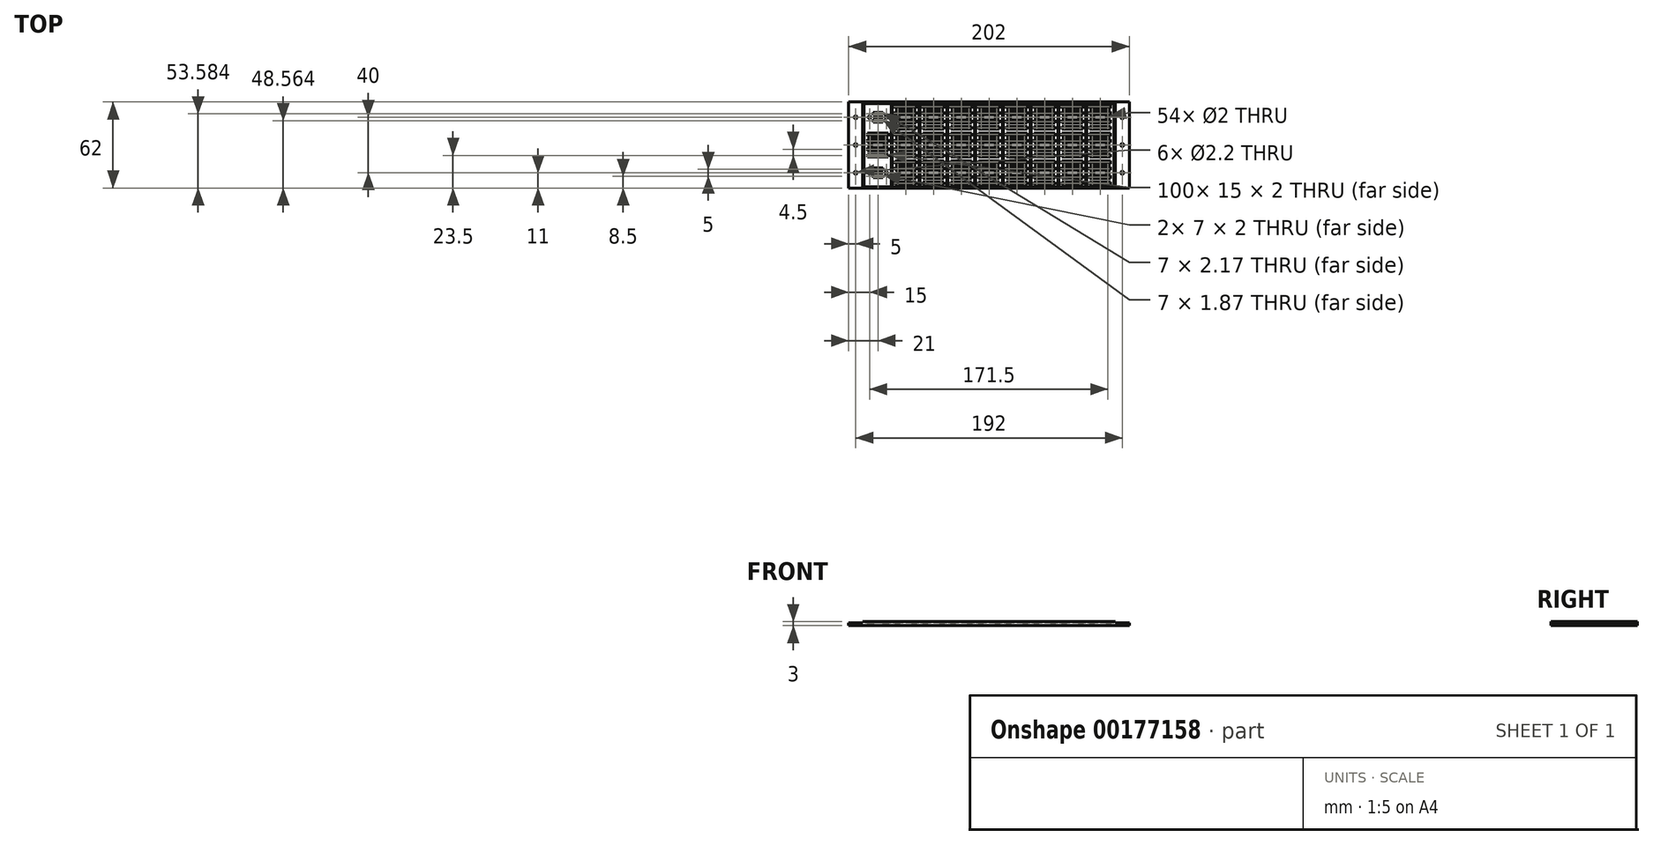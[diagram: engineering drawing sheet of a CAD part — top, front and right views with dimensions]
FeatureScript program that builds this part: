
annotation { "Feature Type Name" : "Feature", "Feature Type Description" : "" }
export const myFeature = defineFeature(function(context is Context, id is Id, definition is map)
    precondition{}
    {
        {
            var Q0;
            Q0=qCreatedBy(makeId("Top.planeOp"),FACE);
            var sketch = newSketch(context, id + "F0", { "sketchPlane" : qUnion([Q0])});
            skLineSegment(sketch, "E0.bottom", {"start": v(91, -31) * mm, "end": v(-91, -31) * mm});
            skLineSegment(sketch, "E0.top", {"start": v(91, 31) * mm, "end": v(-91, 31) * mm});
            skLineSegment(sketch, "E0.left", {"start": v(91, -31) * mm, "end": v(91, 31) * mm});
            skLineSegment(sketch, "E0.right", {"start": v(-91, -31) * mm, "end": v(-91, 31) * mm});
            skPoint(sketch, "E0.middle", {"position": v(0, 0) * mm});
            skSolve(sketch);
        }
        {
            var Q0;
            Q0 = qSketchRegion(id + "F0", true);
            extrude(context, id + "F1", {"entities" : qUnion([Q0]), "depth" : 2 * mm});
        }
        {
            var Q0;
            Q0=makeQuery(id+"F1.opExtrude","CAP_FACE",FACE,{"disambiguationData":[OSD([sQuery(id+"F0.wireOp",EDGE,"E0.bottom"),sQuery(id+"F0.wireOp",EDGE,"E0.top"),sQuery(id+"F0.wireOp",EDGE,"E0.left"),sQuery(id+"F0.wireOp",EDGE,"E0.right")])],"isStart":false});
            var sketch = newSketch(context, id + "F2", { "sketchPlane" : qUnion([Q0])});
            skLineSegment(sketch, "E1.bottom", {"start": v(91, -31) * mm, "end": v(-91, -31) * mm});
            skLineSegment(sketch, "E1.top", {"start": v(91, 31) * mm, "end": v(-91, 31) * mm});
            skLineSegment(sketch, "E1.left", {"start": v(91, -31) * mm, "end": v(91, 31) * mm});
            skLineSegment(sketch, "E1.right", {"start": v(-91, -31) * mm, "end": v(-91, 31) * mm});
            skPoint(sketch, "E1.middle", {"position": v(0, 0) * mm});
            skLineSegment(sketch, "E2.bottom", {"start": v(90, -30) * mm, "end": v(-90, -30) * mm});
            skLineSegment(sketch, "E2.top", {"start": v(90, 30) * mm, "end": v(-90, 30) * mm});
            skLineSegment(sketch, "E2.left", {"start": v(90, -30) * mm, "end": v(90, 30) * mm});
            skLineSegment(sketch, "E2.right", {"start": v(-90, -30) * mm, "end": v(-90, 30) * mm});
            skSolve(sketch);
        }
        {
            var Q0;
            Q0 = qSketchRegion(id + "F2", true);
            extrude(context, id + "F3", {"entities" : qUnion([Q0]), "operationType" : NewBodyOperationType.ADD, "depth" : 1 * mm});
        }
        {
            var Q0;
            Q0=qCreatedBy(makeId("Top.planeOp"),FACE);
            var sketch = newSketch(context, id + "F4", { "sketchPlane" : qUnion([Q0])});
            skLineSegment(sketch, "E3.bottom", {"start": v(-91, 31) * mm, "end": v(-101, 31) * mm});
            skLineSegment(sketch, "E3.top", {"start": v(-91, -31) * mm, "end": v(-101, -31) * mm});
            skLineSegment(sketch, "E3.left", {"start": v(-91, 31) * mm, "end": v(-91, -31) * mm});
            skLineSegment(sketch, "E3.right", {"start": v(-101, 31) * mm, "end": v(-101, -31) * mm});
            skLineSegment(sketch, "E4.bottom", {"start": v(91, 31) * mm, "end": v(101, 31) * mm});
            skLineSegment(sketch, "E4.top", {"start": v(91, -31) * mm, "end": v(101, -31) * mm});
            skLineSegment(sketch, "E4.left", {"start": v(91, 31) * mm, "end": v(91, -31) * mm});
            skLineSegment(sketch, "E4.right", {"start": v(101, 31) * mm, "end": v(101, -31) * mm});
            skCircle(sketch, "E5", {"center": v(-96, 20) * mm, "radius": 1.1 * mm});
            skPoint(sketch, "E5.centerSnap0", {"position": v(-96, 31) * mm});
            skCircle(sketch, "E6", {"center": v(-96, 0) * mm, "radius": 1.1 * mm});
            skCircle(sketch, "E7", {"center": v(-96, -20) * mm, "radius": 1.1 * mm});
            skCircle(sketch, "E8", {"center": v(96, 20) * mm, "radius": 1.1 * mm});
            skPoint(sketch, "E8.centerSnap0", {"position": v(96, 31) * mm});
            skCircle(sketch, "E9", {"center": v(96, 0) * mm, "radius": 1.1 * mm});
            skPoint(sketch, "E9.centerSnap0", {"position": v(91, 0) * mm});
            skCircle(sketch, "E10", {"center": v(96, -20) * mm, "radius": 1.1 * mm});
            skSolve(sketch);
        }
        {
            var Q0;
            Q0 = qSketchRegion(id + "F4", true);
            extrude(context, id + "F5", {"entities" : qUnion([Q0]), "operationType" : NewBodyOperationType.ADD, "depth" : 2 * mm});
        }
        {
            var Q0;
            Q0=makeQuery(id+"F5.boolean.opBoolean","MERGE",FACE,{"derivedFrom":[makeQuery(id+"F1.opExtrude","CAP_FACE",FACE,{"disambiguationData":[OSD([sQuery(id+"F0.wireOp",EDGE,"E0.bottom"),sQuery(id+"F0.wireOp",EDGE,"E0.top"),sQuery(id+"F0.wireOp",EDGE,"E0.left"),sQuery(id+"F0.wireOp",EDGE,"E0.right")])],"isStart":true}),makeQuery(id+"F5.opExtrude","CAP_FACE",FACE,{"disambiguationData":[OSD([sQuery(id+"F4.wireOp",EDGE,"E3.bottom"),sQuery(id+"F4.wireOp",EDGE,"E3.top"),sQuery(id+"F4.wireOp",EDGE,"E3.left"),sQuery(id+"F4.wireOp",EDGE,"E3.right"),sQuery(id+"F4.wireOp",EDGE,"E5"),sQuery(id+"F4.wireOp",EDGE,"E6"),sQuery(id+"F4.wireOp",EDGE,"E7")])],"isStart":true}),makeQuery(id+"F5.opExtrude","CAP_FACE",FACE,{"disambiguationData":[OSD([sQuery(id+"F4.wireOp",EDGE,"E4.bottom"),sQuery(id+"F4.wireOp",EDGE,"E4.top"),sQuery(id+"F4.wireOp",EDGE,"E4.left"),sQuery(id+"F4.wireOp",EDGE,"E4.right"),sQuery(id+"F4.wireOp",EDGE,"E8"),sQuery(id+"F4.wireOp",EDGE,"E9"),sQuery(id+"F4.wireOp",EDGE,"E10")])],"isStart":true})]});
            var sketch = newSketch(context, id + "F6", { "sketchPlane" : qUnion([Q0])});
            skCircle(sketch, "E11", {"center": v(74.5, 20) * mm, "radius": 1 * mm});
            skCircle(sketch, "E12", {"center": v(85.5, 20) * mm, "radius": 1 * mm});
            skLineSegment(sketch, "E13.bottom", {"start": v(87.5, 22) * mm, "end": v(72.5, 22) * mm});
            skLineSegment(sketch, "E13.top", {"start": v(87.5, 24) * mm, "end": v(72.5, 24) * mm});
            skLineSegment(sketch, "E13.left", {"start": v(87.5, 22) * mm, "end": v(87.5, 24) * mm});
            skLineSegment(sketch, "E13.right", {"start": v(72.5, 22) * mm, "end": v(72.5, 24) * mm});
            skPoint(sketch, "E13.middle", {"position": v(80, 23) * mm});
            skLineSegment(sketch, "E14.bottom", {"start": v(87.5, 26.5) * mm, "end": v(72.5, 26.5) * mm});
            skLineSegment(sketch, "E14.top", {"start": v(87.5, 28.5) * mm, "end": v(72.5, 28.5) * mm});
            skLineSegment(sketch, "E14.left", {"start": v(87.5, 26.5) * mm, "end": v(87.5, 28.5) * mm});
            skLineSegment(sketch, "E14.right", {"start": v(72.5, 26.5) * mm, "end": v(72.5, 28.5) * mm});
            skPoint(sketch, "E14.middle", {"position": v(80, 27.5) * mm});
            skLineSegment(sketch, "E15.bottom", {"start": v(87.5, 18) * mm, "end": v(72.5, 18) * mm});
            skLineSegment(sketch, "E15.top", {"start": v(87.5, 16) * mm, "end": v(72.5, 16) * mm});
            skLineSegment(sketch, "E15.left", {"start": v(87.5, 18) * mm, "end": v(87.5, 16) * mm});
            skLineSegment(sketch, "E15.right", {"start": v(72.5, 18) * mm, "end": v(72.5, 16) * mm});
            skPoint(sketch, "E15.middle", {"position": v(80, 17) * mm});
            skLineSegment(sketch, "E16.bottom", {"start": v(87.5, 13.5) * mm, "end": v(72.5, 13.5) * mm});
            skLineSegment(sketch, "E16.top", {"start": v(87.5, 11.5) * mm, "end": v(72.5, 11.5) * mm});
            skLineSegment(sketch, "E16.left", {"start": v(87.5, 13.5) * mm, "end": v(87.5, 11.5) * mm});
            skLineSegment(sketch, "E16.right", {"start": v(72.5, 13.5) * mm, "end": v(72.5, 11.5) * mm});
            skPoint(sketch, "E16.middle", {"position": v(80, 12.5) * mm});
            skLineSegment(sketch, "E17.bottom", {"start": v(89.5, 10.5) * mm, "end": v(70.5, 10.5) * mm, "construction": true});
            skLineSegment(sketch, "E17.top", {"start": v(89.5, 29.5) * mm, "end": v(70.5, 29.5) * mm, "construction": true});
            skLineSegment(sketch, "E17.left", {"start": v(89.5, 10.5) * mm, "end": v(89.5, 29.5) * mm, "construction": true});
            skLineSegment(sketch, "E17.right", {"start": v(70.5, 10.5) * mm, "end": v(70.5, 29.5) * mm, "construction": true});
            skPoint(sketch, "E17.middle", {"position": v(80, 20) * mm});
            skLineSegment(sketch, "E18.0.1.0", {"start": v(87.5, -8.5) * mm, "end": v(72.5, -8.5) * mm});
            skLineSegment(sketch, "E18.0.1.1", {"start": v(87.5, 8.5) * mm, "end": v(72.5, 8.5) * mm});
            skLineSegment(sketch, "E18.0.1.2", {"start": v(87.5, -4) * mm, "end": v(72.5, -4) * mm});
            skLineSegment(sketch, "E18.0.1.3", {"start": v(89.5, -9.5) * mm, "end": v(70.5, -9.5) * mm, "construction": true});
            skPoint(sketch, "E18.0.1.4", {"position": v(80, -3) * mm});
            skLineSegment(sketch, "E18.0.1.5", {"start": v(89.5, 9.5) * mm, "end": v(70.5, 9.5) * mm, "construction": true});
            skLineSegment(sketch, "E18.0.1.6", {"start": v(87.5, 6.5) * mm, "end": v(72.5, 6.5) * mm});
            skLineSegment(sketch, "E18.0.1.7", {"start": v(89.5, -9.5) * mm, "end": v(89.5, 9.5) * mm, "construction": true});
            skPoint(sketch, "E18.0.1.8", {"position": v(80, 3) * mm});
            skLineSegment(sketch, "E18.0.1.9", {"start": v(87.5, -6.5) * mm, "end": v(72.5, -6.5) * mm});
            skLineSegment(sketch, "E18.0.1.10", {"start": v(87.5, 4) * mm, "end": v(72.5, 4) * mm});
            skLineSegment(sketch, "E18.0.1.11", {"start": v(87.5, -2) * mm, "end": v(72.5, -2) * mm});
            skPoint(sketch, "E18.0.1.12", {"position": v(80, 7.5) * mm});
            skLineSegment(sketch, "E18.0.1.13", {"start": v(70.5, -9.5) * mm, "end": v(70.5, 9.5) * mm, "construction": true});
            skPoint(sketch, "E18.0.1.14", {"position": v(80, -7.5) * mm});
            skLineSegment(sketch, "E18.0.1.15", {"start": v(87.5, 2) * mm, "end": v(72.5, 2) * mm});
            skCircle(sketch, "E18.0.1.16", {"center": v(74.5, 0) * mm, "radius": 1 * mm});
            skCircle(sketch, "E18.0.1.17", {"center": v(85.5, 0) * mm, "radius": 1 * mm});
            skPoint(sketch, "E18.0.1.18", {"position": v(80, 0) * mm});
            skLineSegment(sketch, "E18.0.1.19", {"start": v(72.5, -6.5) * mm, "end": v(72.5, -8.5) * mm});
            skLineSegment(sketch, "E18.0.1.20", {"start": v(87.5, 6.5) * mm, "end": v(87.5, 8.5) * mm});
            skLineSegment(sketch, "E18.0.1.21", {"start": v(72.5, 6.5) * mm, "end": v(72.5, 8.5) * mm});
            skLineSegment(sketch, "E18.0.1.22", {"start": v(87.5, -2) * mm, "end": v(87.5, -4) * mm});
            skLineSegment(sketch, "E18.0.1.23", {"start": v(87.5, 2) * mm, "end": v(87.5, 4) * mm});
            skLineSegment(sketch, "E18.0.1.24", {"start": v(72.5, 2) * mm, "end": v(72.5, 4) * mm});
            skLineSegment(sketch, "E18.0.1.25", {"start": v(87.5, -6.5) * mm, "end": v(87.5, -8.5) * mm});
            skLineSegment(sketch, "E18.0.1.26", {"start": v(72.5, -2) * mm, "end": v(72.5, -4) * mm});
            skLineSegment(sketch, "E18.0.2.0", {"start": v(87.5, -28.5) * mm, "end": v(72.5, -28.5) * mm});
            skLineSegment(sketch, "E18.0.2.1", {"start": v(87.5, -11.5) * mm, "end": v(72.5, -11.5) * mm});
            skLineSegment(sketch, "E18.0.2.2", {"start": v(87.5, -24) * mm, "end": v(72.5, -24) * mm});
            skLineSegment(sketch, "E18.0.2.3", {"start": v(89.5, -29.5) * mm, "end": v(70.5, -29.5) * mm, "construction": true});
            skPoint(sketch, "E18.0.2.4", {"position": v(80, -23) * mm});
            skLineSegment(sketch, "E18.0.2.5", {"start": v(89.5, -10.5) * mm, "end": v(70.5, -10.5) * mm, "construction": true});
            skLineSegment(sketch, "E18.0.2.6", {"start": v(87.5, -13.5) * mm, "end": v(72.5, -13.5) * mm});
            skLineSegment(sketch, "E18.0.2.7", {"start": v(89.5, -29.5) * mm, "end": v(89.5, -10.5) * mm, "construction": true});
            skPoint(sketch, "E18.0.2.8", {"position": v(80, -17) * mm});
            skLineSegment(sketch, "E18.0.2.9", {"start": v(87.5, -26.5) * mm, "end": v(72.5, -26.5) * mm});
            skLineSegment(sketch, "E18.0.2.10", {"start": v(87.5, -16) * mm, "end": v(72.5, -16) * mm});
            skLineSegment(sketch, "E18.0.2.11", {"start": v(87.5, -22) * mm, "end": v(72.5, -22) * mm});
            skPoint(sketch, "E18.0.2.12", {"position": v(80, -12.5) * mm});
            skLineSegment(sketch, "E18.0.2.13", {"start": v(70.5, -29.5) * mm, "end": v(70.5, -10.5) * mm, "construction": true});
            skPoint(sketch, "E18.0.2.14", {"position": v(80, -27.5) * mm});
            skLineSegment(sketch, "E18.0.2.15", {"start": v(87.5, -18) * mm, "end": v(72.5, -18) * mm});
            skCircle(sketch, "E18.0.2.16", {"center": v(74.5, -20) * mm, "radius": 1 * mm});
            skCircle(sketch, "E18.0.2.17", {"center": v(85.5, -20) * mm, "radius": 1 * mm});
            skPoint(sketch, "E18.0.2.18", {"position": v(80, -20) * mm});
            skLineSegment(sketch, "E18.0.2.19", {"start": v(72.5, -26.5) * mm, "end": v(72.5, -28.5) * mm});
            skLineSegment(sketch, "E18.0.2.20", {"start": v(87.5, -13.5) * mm, "end": v(87.5, -11.5) * mm});
            skLineSegment(sketch, "E18.0.2.21", {"start": v(72.5, -13.5) * mm, "end": v(72.5, -11.5) * mm});
            skLineSegment(sketch, "E18.0.2.22", {"start": v(87.5, -22) * mm, "end": v(87.5, -24) * mm});
            skLineSegment(sketch, "E18.0.2.23", {"start": v(87.5, -18) * mm, "end": v(87.5, -16) * mm});
            skLineSegment(sketch, "E18.0.2.24", {"start": v(72.5, -18) * mm, "end": v(72.5, -16) * mm});
            skLineSegment(sketch, "E18.0.2.25", {"start": v(87.5, -26.5) * mm, "end": v(87.5, -28.5) * mm});
            skLineSegment(sketch, "E18.0.2.26", {"start": v(72.5, -22) * mm, "end": v(72.5, -24) * mm});
            skLineSegment(sketch, "E18.1.0.0", {"start": v(67.5, 11.5) * mm, "end": v(52.5, 11.5) * mm});
            skLineSegment(sketch, "E18.1.0.1", {"start": v(67.5, 28.5) * mm, "end": v(52.5, 28.5) * mm});
            skLineSegment(sketch, "E18.1.0.2", {"start": v(67.5, 16) * mm, "end": v(52.5, 16) * mm});
            skLineSegment(sketch, "E18.1.0.3", {"start": v(69.5, 10.5) * mm, "end": v(50.5, 10.5) * mm, "construction": true});
            skPoint(sketch, "E18.1.0.4", {"position": v(60, 17) * mm});
            skLineSegment(sketch, "E18.1.0.5", {"start": v(69.5, 29.5) * mm, "end": v(50.5, 29.5) * mm, "construction": true});
            skLineSegment(sketch, "E18.1.0.6", {"start": v(67.5, 26.5) * mm, "end": v(52.5, 26.5) * mm});
            skLineSegment(sketch, "E18.1.0.7", {"start": v(69.5, 10.5) * mm, "end": v(69.5, 29.5) * mm, "construction": true});
            skPoint(sketch, "E18.1.0.8", {"position": v(60, 23) * mm});
            skLineSegment(sketch, "E18.1.0.9", {"start": v(67.5, 13.5) * mm, "end": v(52.5, 13.5) * mm});
            skLineSegment(sketch, "E18.1.0.10", {"start": v(67.5, 24) * mm, "end": v(52.5, 24) * mm});
            skLineSegment(sketch, "E18.1.0.11", {"start": v(67.5, 18) * mm, "end": v(52.5, 18) * mm});
            skPoint(sketch, "E18.1.0.12", {"position": v(60, 27.5) * mm});
            skLineSegment(sketch, "E18.1.0.13", {"start": v(50.5, 10.5) * mm, "end": v(50.5, 29.5) * mm, "construction": true});
            skPoint(sketch, "E18.1.0.14", {"position": v(60, 12.5) * mm});
            skLineSegment(sketch, "E18.1.0.15", {"start": v(67.5, 22) * mm, "end": v(52.5, 22) * mm});
            skCircle(sketch, "E18.1.0.16", {"center": v(54.5, 20) * mm, "radius": 1 * mm});
            skCircle(sketch, "E18.1.0.17", {"center": v(65.5, 20) * mm, "radius": 1 * mm});
            skPoint(sketch, "E18.1.0.18", {"position": v(60, 20) * mm});
            skLineSegment(sketch, "E18.1.0.19", {"start": v(52.5, 13.5) * mm, "end": v(52.5, 11.5) * mm});
            skLineSegment(sketch, "E18.1.0.20", {"start": v(67.5, 26.5) * mm, "end": v(67.5, 28.5) * mm});
            skLineSegment(sketch, "E18.1.0.21", {"start": v(52.5, 26.5) * mm, "end": v(52.5, 28.5) * mm});
            skLineSegment(sketch, "E18.1.0.22", {"start": v(67.5, 18) * mm, "end": v(67.5, 16) * mm});
            skLineSegment(sketch, "E18.1.0.23", {"start": v(67.5, 22) * mm, "end": v(67.5, 24) * mm});
            skLineSegment(sketch, "E18.1.0.24", {"start": v(52.5, 22) * mm, "end": v(52.5, 24) * mm});
            skLineSegment(sketch, "E18.1.0.25", {"start": v(67.5, 13.5) * mm, "end": v(67.5, 11.5) * mm});
            skLineSegment(sketch, "E18.1.0.26", {"start": v(52.5, 18) * mm, "end": v(52.5, 16) * mm});
            skLineSegment(sketch, "E18.1.1.0", {"start": v(67.5, -8.5) * mm, "end": v(52.5, -8.5) * mm});
            skLineSegment(sketch, "E18.1.1.1", {"start": v(67.5, 8.5) * mm, "end": v(52.5, 8.5) * mm});
            skLineSegment(sketch, "E18.1.1.2", {"start": v(67.5, -4) * mm, "end": v(52.5, -4) * mm});
            skLineSegment(sketch, "E18.1.1.3", {"start": v(69.5, -9.5) * mm, "end": v(50.5, -9.5) * mm, "construction": true});
            skPoint(sketch, "E18.1.1.4", {"position": v(60, -3) * mm});
            skLineSegment(sketch, "E18.1.1.5", {"start": v(69.5, 9.5) * mm, "end": v(50.5, 9.5) * mm, "construction": true});
            skLineSegment(sketch, "E18.1.1.6", {"start": v(67.5, 6.5) * mm, "end": v(52.5, 6.5) * mm});
            skLineSegment(sketch, "E18.1.1.7", {"start": v(69.5, -9.5) * mm, "end": v(69.5, 9.5) * mm, "construction": true});
            skPoint(sketch, "E18.1.1.8", {"position": v(60, 3) * mm});
            skLineSegment(sketch, "E18.1.1.9", {"start": v(67.5, -6.5) * mm, "end": v(52.5, -6.5) * mm});
            skLineSegment(sketch, "E18.1.1.10", {"start": v(67.5, 4) * mm, "end": v(52.5, 4) * mm});
            skLineSegment(sketch, "E18.1.1.11", {"start": v(67.5, -2) * mm, "end": v(52.5, -2) * mm});
            skPoint(sketch, "E18.1.1.12", {"position": v(60, 7.5) * mm});
            skLineSegment(sketch, "E18.1.1.13", {"start": v(50.5, -9.5) * mm, "end": v(50.5, 9.5) * mm, "construction": true});
            skPoint(sketch, "E18.1.1.14", {"position": v(60, -7.5) * mm});
            skLineSegment(sketch, "E18.1.1.15", {"start": v(67.5, 2) * mm, "end": v(52.5, 2) * mm});
            skCircle(sketch, "E18.1.1.16", {"center": v(54.5, 0) * mm, "radius": 1 * mm});
            skCircle(sketch, "E18.1.1.17", {"center": v(65.5, 0) * mm, "radius": 1 * mm});
            skPoint(sketch, "E18.1.1.18", {"position": v(60, 0) * mm});
            skLineSegment(sketch, "E18.1.1.19", {"start": v(52.5, -6.5) * mm, "end": v(52.5, -8.5) * mm});
            skLineSegment(sketch, "E18.1.1.20", {"start": v(67.5, 6.5) * mm, "end": v(67.5, 8.5) * mm});
            skLineSegment(sketch, "E18.1.1.21", {"start": v(52.5, 6.5) * mm, "end": v(52.5, 8.5) * mm});
            skLineSegment(sketch, "E18.1.1.22", {"start": v(67.5, -2) * mm, "end": v(67.5, -4) * mm});
            skLineSegment(sketch, "E18.1.1.23", {"start": v(67.5, 2) * mm, "end": v(67.5, 4) * mm});
            skLineSegment(sketch, "E18.1.1.24", {"start": v(52.5, 2) * mm, "end": v(52.5, 4) * mm});
            skLineSegment(sketch, "E18.1.1.25", {"start": v(67.5, -6.5) * mm, "end": v(67.5, -8.5) * mm});
            skLineSegment(sketch, "E18.1.1.26", {"start": v(52.5, -2) * mm, "end": v(52.5, -4) * mm});
            skLineSegment(sketch, "E18.1.2.0", {"start": v(67.5, -28.5) * mm, "end": v(52.5, -28.5) * mm});
            skLineSegment(sketch, "E18.1.2.1", {"start": v(67.5, -11.5) * mm, "end": v(52.5, -11.5) * mm});
            skLineSegment(sketch, "E18.1.2.2", {"start": v(67.5, -24) * mm, "end": v(52.5, -24) * mm});
            skLineSegment(sketch, "E18.1.2.3", {"start": v(69.5, -29.5) * mm, "end": v(50.5, -29.5) * mm, "construction": true});
            skPoint(sketch, "E18.1.2.4", {"position": v(60, -23) * mm});
            skLineSegment(sketch, "E18.1.2.5", {"start": v(69.5, -10.5) * mm, "end": v(50.5, -10.5) * mm, "construction": true});
            skLineSegment(sketch, "E18.1.2.6", {"start": v(67.5, -13.5) * mm, "end": v(52.5, -13.5) * mm});
            skLineSegment(sketch, "E18.1.2.7", {"start": v(69.5, -29.5) * mm, "end": v(69.5, -10.5) * mm, "construction": true});
            skPoint(sketch, "E18.1.2.8", {"position": v(60, -17) * mm});
            skLineSegment(sketch, "E18.1.2.9", {"start": v(67.5, -26.5) * mm, "end": v(52.5, -26.5) * mm});
            skLineSegment(sketch, "E18.1.2.10", {"start": v(67.5, -16) * mm, "end": v(52.5, -16) * mm});
            skLineSegment(sketch, "E18.1.2.11", {"start": v(67.5, -22) * mm, "end": v(52.5, -22) * mm});
            skPoint(sketch, "E18.1.2.12", {"position": v(60, -12.5) * mm});
            skLineSegment(sketch, "E18.1.2.13", {"start": v(50.5, -29.5) * mm, "end": v(50.5, -10.5) * mm, "construction": true});
            skPoint(sketch, "E18.1.2.14", {"position": v(60, -27.5) * mm});
            skLineSegment(sketch, "E18.1.2.15", {"start": v(67.5, -18) * mm, "end": v(52.5, -18) * mm});
            skCircle(sketch, "E18.1.2.16", {"center": v(54.5, -20) * mm, "radius": 1 * mm});
            skCircle(sketch, "E18.1.2.17", {"center": v(65.5, -20) * mm, "radius": 1 * mm});
            skPoint(sketch, "E18.1.2.18", {"position": v(60, -20) * mm});
            skLineSegment(sketch, "E18.1.2.19", {"start": v(52.5, -26.5) * mm, "end": v(52.5, -28.5) * mm});
            skLineSegment(sketch, "E18.1.2.20", {"start": v(67.5, -13.5) * mm, "end": v(67.5, -11.5) * mm});
            skLineSegment(sketch, "E18.1.2.21", {"start": v(52.5, -13.5) * mm, "end": v(52.5, -11.5) * mm});
            skLineSegment(sketch, "E18.1.2.22", {"start": v(67.5, -22) * mm, "end": v(67.5, -24) * mm});
            skLineSegment(sketch, "E18.1.2.23", {"start": v(67.5, -18) * mm, "end": v(67.5, -16) * mm});
            skLineSegment(sketch, "E18.1.2.24", {"start": v(52.5, -18) * mm, "end": v(52.5, -16) * mm});
            skLineSegment(sketch, "E18.1.2.25", {"start": v(67.5, -26.5) * mm, "end": v(67.5, -28.5) * mm});
            skLineSegment(sketch, "E18.1.2.26", {"start": v(52.5, -22) * mm, "end": v(52.5, -24) * mm});
            skLineSegment(sketch, "E18.2.0.0", {"start": v(47.5, 11.5) * mm, "end": v(32.5, 11.5) * mm});
            skLineSegment(sketch, "E18.2.0.1", {"start": v(47.5, 28.5) * mm, "end": v(32.5, 28.5) * mm});
            skLineSegment(sketch, "E18.2.0.2", {"start": v(47.5, 16) * mm, "end": v(32.5, 16) * mm});
            skLineSegment(sketch, "E18.2.0.3", {"start": v(49.5, 10.5) * mm, "end": v(30.5, 10.5) * mm, "construction": true});
            skPoint(sketch, "E18.2.0.4", {"position": v(40, 17) * mm});
            skLineSegment(sketch, "E18.2.0.5", {"start": v(49.5, 29.5) * mm, "end": v(30.5, 29.5) * mm, "construction": true});
            skLineSegment(sketch, "E18.2.0.6", {"start": v(47.5, 26.5) * mm, "end": v(32.5, 26.5) * mm});
            skLineSegment(sketch, "E18.2.0.7", {"start": v(49.5, 10.5) * mm, "end": v(49.5, 29.5) * mm, "construction": true});
            skPoint(sketch, "E18.2.0.8", {"position": v(40, 23) * mm});
            skLineSegment(sketch, "E18.2.0.9", {"start": v(47.5, 13.5) * mm, "end": v(32.5, 13.5) * mm});
            skLineSegment(sketch, "E18.2.0.10", {"start": v(47.5, 24) * mm, "end": v(32.5, 24) * mm});
            skLineSegment(sketch, "E18.2.0.11", {"start": v(47.5, 18) * mm, "end": v(32.5, 18) * mm});
            skPoint(sketch, "E18.2.0.12", {"position": v(40, 27.5) * mm});
            skLineSegment(sketch, "E18.2.0.13", {"start": v(30.5, 10.5) * mm, "end": v(30.5, 29.5) * mm, "construction": true});
            skPoint(sketch, "E18.2.0.14", {"position": v(40, 12.5) * mm});
            skLineSegment(sketch, "E18.2.0.15", {"start": v(47.5, 22) * mm, "end": v(32.5, 22) * mm});
            skCircle(sketch, "E18.2.0.16", {"center": v(34.5, 20) * mm, "radius": 1 * mm});
            skCircle(sketch, "E18.2.0.17", {"center": v(45.5, 20) * mm, "radius": 1 * mm});
            skPoint(sketch, "E18.2.0.18", {"position": v(40, 20) * mm});
            skLineSegment(sketch, "E18.2.0.19", {"start": v(32.5, 13.5) * mm, "end": v(32.5, 11.5) * mm});
            skLineSegment(sketch, "E18.2.0.20", {"start": v(47.5, 26.5) * mm, "end": v(47.5, 28.5) * mm});
            skLineSegment(sketch, "E18.2.0.21", {"start": v(32.5, 26.5) * mm, "end": v(32.5, 28.5) * mm});
            skLineSegment(sketch, "E18.2.0.22", {"start": v(47.5, 18) * mm, "end": v(47.5, 16) * mm});
            skLineSegment(sketch, "E18.2.0.23", {"start": v(47.5, 22) * mm, "end": v(47.5, 24) * mm});
            skLineSegment(sketch, "E18.2.0.24", {"start": v(32.5, 22) * mm, "end": v(32.5, 24) * mm});
            skLineSegment(sketch, "E18.2.0.25", {"start": v(47.5, 13.5) * mm, "end": v(47.5, 11.5) * mm});
            skLineSegment(sketch, "E18.2.0.26", {"start": v(32.5, 18) * mm, "end": v(32.5, 16) * mm});
            skLineSegment(sketch, "E18.2.1.0", {"start": v(47.5, -8.5) * mm, "end": v(32.5, -8.5) * mm});
            skLineSegment(sketch, "E18.2.1.1", {"start": v(47.5, 8.5) * mm, "end": v(32.5, 8.5) * mm});
            skLineSegment(sketch, "E18.2.1.2", {"start": v(47.5, -4) * mm, "end": v(32.5, -4) * mm});
            skLineSegment(sketch, "E18.2.1.3", {"start": v(49.5, -9.5) * mm, "end": v(30.5, -9.5) * mm, "construction": true});
            skPoint(sketch, "E18.2.1.4", {"position": v(40, -3) * mm});
            skLineSegment(sketch, "E18.2.1.5", {"start": v(49.5, 9.5) * mm, "end": v(30.5, 9.5) * mm, "construction": true});
            skLineSegment(sketch, "E18.2.1.6", {"start": v(47.5, 6.5) * mm, "end": v(32.5, 6.5) * mm});
            skLineSegment(sketch, "E18.2.1.7", {"start": v(49.5, -9.5) * mm, "end": v(49.5, 9.5) * mm, "construction": true});
            skPoint(sketch, "E18.2.1.8", {"position": v(40, 3) * mm});
            skLineSegment(sketch, "E18.2.1.9", {"start": v(47.5, -6.5) * mm, "end": v(32.5, -6.5) * mm});
            skLineSegment(sketch, "E18.2.1.10", {"start": v(47.5, 4) * mm, "end": v(32.5, 4) * mm});
            skLineSegment(sketch, "E18.2.1.11", {"start": v(47.5, -2) * mm, "end": v(32.5, -2) * mm});
            skPoint(sketch, "E18.2.1.12", {"position": v(40, 7.5) * mm});
            skLineSegment(sketch, "E18.2.1.13", {"start": v(30.5, -9.5) * mm, "end": v(30.5, 9.5) * mm, "construction": true});
            skPoint(sketch, "E18.2.1.14", {"position": v(40, -7.5) * mm});
            skLineSegment(sketch, "E18.2.1.15", {"start": v(47.5, 2) * mm, "end": v(32.5, 2) * mm});
            skCircle(sketch, "E18.2.1.16", {"center": v(34.5, 0) * mm, "radius": 1 * mm});
            skCircle(sketch, "E18.2.1.17", {"center": v(45.5, 0) * mm, "radius": 1 * mm});
            skPoint(sketch, "E18.2.1.18", {"position": v(40, 0) * mm});
            skLineSegment(sketch, "E18.2.1.19", {"start": v(32.5, -6.5) * mm, "end": v(32.5, -8.5) * mm});
            skLineSegment(sketch, "E18.2.1.20", {"start": v(47.5, 6.5) * mm, "end": v(47.5, 8.5) * mm});
            skLineSegment(sketch, "E18.2.1.21", {"start": v(32.5, 6.5) * mm, "end": v(32.5, 8.5) * mm});
            skLineSegment(sketch, "E18.2.1.22", {"start": v(47.5, -2) * mm, "end": v(47.5, -4) * mm});
            skLineSegment(sketch, "E18.2.1.23", {"start": v(47.5, 2) * mm, "end": v(47.5, 4) * mm});
            skLineSegment(sketch, "E18.2.1.24", {"start": v(32.5, 2) * mm, "end": v(32.5, 4) * mm});
            skLineSegment(sketch, "E18.2.1.25", {"start": v(47.5, -6.5) * mm, "end": v(47.5, -8.5) * mm});
            skLineSegment(sketch, "E18.2.1.26", {"start": v(32.5, -2) * mm, "end": v(32.5, -4) * mm});
            skLineSegment(sketch, "E18.2.2.0", {"start": v(47.5, -28.5) * mm, "end": v(32.5, -28.5) * mm});
            skLineSegment(sketch, "E18.2.2.1", {"start": v(47.5, -11.5) * mm, "end": v(32.5, -11.5) * mm});
            skLineSegment(sketch, "E18.2.2.2", {"start": v(47.5, -24) * mm, "end": v(32.5, -24) * mm});
            skLineSegment(sketch, "E18.2.2.3", {"start": v(49.5, -29.5) * mm, "end": v(30.5, -29.5) * mm, "construction": true});
            skPoint(sketch, "E18.2.2.4", {"position": v(40, -23) * mm});
            skLineSegment(sketch, "E18.2.2.5", {"start": v(49.5, -10.5) * mm, "end": v(30.5, -10.5) * mm, "construction": true});
            skLineSegment(sketch, "E18.2.2.6", {"start": v(47.5, -13.5) * mm, "end": v(32.5, -13.5) * mm});
            skLineSegment(sketch, "E18.2.2.7", {"start": v(49.5, -29.5) * mm, "end": v(49.5, -10.5) * mm, "construction": true});
            skPoint(sketch, "E18.2.2.8", {"position": v(40, -17) * mm});
            skLineSegment(sketch, "E18.2.2.9", {"start": v(47.5, -26.5) * mm, "end": v(32.5, -26.5) * mm});
            skLineSegment(sketch, "E18.2.2.10", {"start": v(47.5, -16) * mm, "end": v(32.5, -16) * mm});
            skLineSegment(sketch, "E18.2.2.11", {"start": v(47.5, -22) * mm, "end": v(32.5, -22) * mm});
            skPoint(sketch, "E18.2.2.12", {"position": v(40, -12.5) * mm});
            skLineSegment(sketch, "E18.2.2.13", {"start": v(30.5, -29.5) * mm, "end": v(30.5, -10.5) * mm, "construction": true});
            skPoint(sketch, "E18.2.2.14", {"position": v(40, -27.5) * mm});
            skLineSegment(sketch, "E18.2.2.15", {"start": v(47.5, -18) * mm, "end": v(32.5, -18) * mm});
            skCircle(sketch, "E18.2.2.16", {"center": v(34.5, -20) * mm, "radius": 1 * mm});
            skCircle(sketch, "E18.2.2.17", {"center": v(45.5, -20) * mm, "radius": 1 * mm});
            skPoint(sketch, "E18.2.2.18", {"position": v(40, -20) * mm});
            skLineSegment(sketch, "E18.2.2.19", {"start": v(32.5, -26.5) * mm, "end": v(32.5, -28.5) * mm});
            skLineSegment(sketch, "E18.2.2.20", {"start": v(47.5, -13.5) * mm, "end": v(47.5, -11.5) * mm});
            skLineSegment(sketch, "E18.2.2.21", {"start": v(32.5, -13.5) * mm, "end": v(32.5, -11.5) * mm});
            skLineSegment(sketch, "E18.2.2.22", {"start": v(47.5, -22) * mm, "end": v(47.5, -24) * mm});
            skLineSegment(sketch, "E18.2.2.23", {"start": v(47.5, -18) * mm, "end": v(47.5, -16) * mm});
            skLineSegment(sketch, "E18.2.2.24", {"start": v(32.5, -18) * mm, "end": v(32.5, -16) * mm});
            skLineSegment(sketch, "E18.2.2.25", {"start": v(47.5, -26.5) * mm, "end": v(47.5, -28.5) * mm});
            skLineSegment(sketch, "E18.2.2.26", {"start": v(32.5, -22) * mm, "end": v(32.5, -24) * mm});
            skLineSegment(sketch, "E18.3.0.0", {"start": v(27.5, 11.5) * mm, "end": v(12.5, 11.5) * mm});
            skLineSegment(sketch, "E18.3.0.1", {"start": v(27.5, 28.5) * mm, "end": v(12.5, 28.5) * mm});
            skLineSegment(sketch, "E18.3.0.2", {"start": v(27.5, 16) * mm, "end": v(12.5, 16) * mm});
            skLineSegment(sketch, "E18.3.0.3", {"start": v(29.5, 10.5) * mm, "end": v(10.5, 10.5) * mm, "construction": true});
            skPoint(sketch, "E18.3.0.4", {"position": v(20, 17) * mm});
            skLineSegment(sketch, "E18.3.0.5", {"start": v(29.5, 29.5) * mm, "end": v(10.5, 29.5) * mm, "construction": true});
            skLineSegment(sketch, "E18.3.0.6", {"start": v(27.5, 26.5) * mm, "end": v(12.5, 26.5) * mm});
            skLineSegment(sketch, "E18.3.0.7", {"start": v(29.5, 10.5) * mm, "end": v(29.5, 29.5) * mm, "construction": true});
            skPoint(sketch, "E18.3.0.8", {"position": v(20, 23) * mm});
            skLineSegment(sketch, "E18.3.0.9", {"start": v(27.5, 13.5) * mm, "end": v(12.5, 13.5) * mm});
            skLineSegment(sketch, "E18.3.0.10", {"start": v(27.5, 24) * mm, "end": v(12.5, 24) * mm});
            skLineSegment(sketch, "E18.3.0.11", {"start": v(27.5, 18) * mm, "end": v(12.5, 18) * mm});
            skPoint(sketch, "E18.3.0.12", {"position": v(20, 27.5) * mm});
            skLineSegment(sketch, "E18.3.0.13", {"start": v(10.5, 10.5) * mm, "end": v(10.5, 29.5) * mm, "construction": true});
            skPoint(sketch, "E18.3.0.14", {"position": v(20, 12.5) * mm});
            skLineSegment(sketch, "E18.3.0.15", {"start": v(27.5, 22) * mm, "end": v(12.5, 22) * mm});
            skCircle(sketch, "E18.3.0.16", {"center": v(14.5, 20) * mm, "radius": 1 * mm});
            skCircle(sketch, "E18.3.0.17", {"center": v(25.5, 20) * mm, "radius": 1 * mm});
            skPoint(sketch, "E18.3.0.18", {"position": v(20, 20) * mm});
            skLineSegment(sketch, "E18.3.0.19", {"start": v(12.5, 13.5) * mm, "end": v(12.5, 11.5) * mm});
            skLineSegment(sketch, "E18.3.0.20", {"start": v(27.5, 26.5) * mm, "end": v(27.5, 28.5) * mm});
            skLineSegment(sketch, "E18.3.0.21", {"start": v(12.5, 26.5) * mm, "end": v(12.5, 28.5) * mm});
            skLineSegment(sketch, "E18.3.0.22", {"start": v(27.5, 18) * mm, "end": v(27.5, 16) * mm});
            skLineSegment(sketch, "E18.3.0.23", {"start": v(27.5, 22) * mm, "end": v(27.5, 24) * mm});
            skLineSegment(sketch, "E18.3.0.24", {"start": v(12.5, 22) * mm, "end": v(12.5, 24) * mm});
            skLineSegment(sketch, "E18.3.0.25", {"start": v(27.5, 13.5) * mm, "end": v(27.5, 11.5) * mm});
            skLineSegment(sketch, "E18.3.0.26", {"start": v(12.5, 18) * mm, "end": v(12.5, 16) * mm});
            skLineSegment(sketch, "E18.3.1.0", {"start": v(27.5, -8.5) * mm, "end": v(12.5, -8.5) * mm});
            skLineSegment(sketch, "E18.3.1.1", {"start": v(27.5, 8.5) * mm, "end": v(12.5, 8.5) * mm});
            skLineSegment(sketch, "E18.3.1.2", {"start": v(27.5, -4) * mm, "end": v(12.5, -4) * mm});
            skLineSegment(sketch, "E18.3.1.3", {"start": v(29.5, -9.5) * mm, "end": v(10.5, -9.5) * mm, "construction": true});
            skPoint(sketch, "E18.3.1.4", {"position": v(20, -3) * mm});
            skLineSegment(sketch, "E18.3.1.5", {"start": v(29.5, 9.5) * mm, "end": v(10.5, 9.5) * mm, "construction": true});
            skLineSegment(sketch, "E18.3.1.6", {"start": v(27.5, 6.5) * mm, "end": v(12.5, 6.5) * mm});
            skLineSegment(sketch, "E18.3.1.7", {"start": v(29.5, -9.5) * mm, "end": v(29.5, 9.5) * mm, "construction": true});
            skPoint(sketch, "E18.3.1.8", {"position": v(20, 3) * mm});
            skLineSegment(sketch, "E18.3.1.9", {"start": v(27.5, -6.5) * mm, "end": v(12.5, -6.5) * mm});
            skLineSegment(sketch, "E18.3.1.10", {"start": v(27.5, 4) * mm, "end": v(12.5, 4) * mm});
            skLineSegment(sketch, "E18.3.1.11", {"start": v(27.5, -2) * mm, "end": v(12.5, -2) * mm});
            skPoint(sketch, "E18.3.1.12", {"position": v(20, 7.5) * mm});
            skLineSegment(sketch, "E18.3.1.13", {"start": v(10.5, -9.5) * mm, "end": v(10.5, 9.5) * mm, "construction": true});
            skPoint(sketch, "E18.3.1.14", {"position": v(20, -7.5) * mm});
            skLineSegment(sketch, "E18.3.1.15", {"start": v(27.5, 2) * mm, "end": v(12.5, 2) * mm});
            skCircle(sketch, "E18.3.1.16", {"center": v(14.5, 0) * mm, "radius": 1 * mm});
            skCircle(sketch, "E18.3.1.17", {"center": v(25.5, 0) * mm, "radius": 1 * mm});
            skPoint(sketch, "E18.3.1.18", {"position": v(20, 0) * mm});
            skLineSegment(sketch, "E18.3.1.19", {"start": v(12.5, -6.5) * mm, "end": v(12.5, -8.5) * mm});
            skLineSegment(sketch, "E18.3.1.20", {"start": v(27.5, 6.5) * mm, "end": v(27.5, 8.5) * mm});
            skLineSegment(sketch, "E18.3.1.21", {"start": v(12.5, 6.5) * mm, "end": v(12.5, 8.5) * mm});
            skLineSegment(sketch, "E18.3.1.22", {"start": v(27.5, -2) * mm, "end": v(27.5, -4) * mm});
            skLineSegment(sketch, "E18.3.1.23", {"start": v(27.5, 2) * mm, "end": v(27.5, 4) * mm});
            skLineSegment(sketch, "E18.3.1.24", {"start": v(12.5, 2) * mm, "end": v(12.5, 4) * mm});
            skLineSegment(sketch, "E18.3.1.25", {"start": v(27.5, -6.5) * mm, "end": v(27.5, -8.5) * mm});
            skLineSegment(sketch, "E18.3.1.26", {"start": v(12.5, -2) * mm, "end": v(12.5, -4) * mm});
            skLineSegment(sketch, "E18.3.2.0", {"start": v(27.5, -28.5) * mm, "end": v(12.5, -28.5) * mm});
            skLineSegment(sketch, "E18.3.2.1", {"start": v(27.5, -11.5) * mm, "end": v(12.5, -11.5) * mm});
            skLineSegment(sketch, "E18.3.2.2", {"start": v(27.5, -24) * mm, "end": v(12.5, -24) * mm});
            skLineSegment(sketch, "E18.3.2.3", {"start": v(29.5, -29.5) * mm, "end": v(10.5, -29.5) * mm, "construction": true});
            skPoint(sketch, "E18.3.2.4", {"position": v(20, -23) * mm});
            skLineSegment(sketch, "E18.3.2.5", {"start": v(29.5, -10.5) * mm, "end": v(10.5, -10.5) * mm, "construction": true});
            skLineSegment(sketch, "E18.3.2.6", {"start": v(27.5, -13.5) * mm, "end": v(12.5, -13.5) * mm});
            skLineSegment(sketch, "E18.3.2.7", {"start": v(29.5, -29.5) * mm, "end": v(29.5, -10.5) * mm, "construction": true});
            skPoint(sketch, "E18.3.2.8", {"position": v(20, -17) * mm});
            skLineSegment(sketch, "E18.3.2.9", {"start": v(27.5, -26.5) * mm, "end": v(12.5, -26.5) * mm});
            skLineSegment(sketch, "E18.3.2.10", {"start": v(27.5, -16) * mm, "end": v(12.5, -16) * mm});
            skLineSegment(sketch, "E18.3.2.11", {"start": v(27.5, -22) * mm, "end": v(12.5, -22) * mm});
            skPoint(sketch, "E18.3.2.12", {"position": v(20, -12.5) * mm});
            skLineSegment(sketch, "E18.3.2.13", {"start": v(10.5, -29.5) * mm, "end": v(10.5, -10.5) * mm, "construction": true});
            skPoint(sketch, "E18.3.2.14", {"position": v(20, -27.5) * mm});
            skLineSegment(sketch, "E18.3.2.15", {"start": v(27.5, -18) * mm, "end": v(12.5, -18) * mm});
            skCircle(sketch, "E18.3.2.16", {"center": v(14.5, -20) * mm, "radius": 1 * mm});
            skCircle(sketch, "E18.3.2.17", {"center": v(25.5, -20) * mm, "radius": 1 * mm});
            skPoint(sketch, "E18.3.2.18", {"position": v(20, -20) * mm});
            skLineSegment(sketch, "E18.3.2.19", {"start": v(12.5, -26.5) * mm, "end": v(12.5, -28.5) * mm});
            skLineSegment(sketch, "E18.3.2.20", {"start": v(27.5, -13.5) * mm, "end": v(27.5, -11.5) * mm});
            skLineSegment(sketch, "E18.3.2.21", {"start": v(12.5, -13.5) * mm, "end": v(12.5, -11.5) * mm});
            skLineSegment(sketch, "E18.3.2.22", {"start": v(27.5, -22) * mm, "end": v(27.5, -24) * mm});
            skLineSegment(sketch, "E18.3.2.23", {"start": v(27.5, -18) * mm, "end": v(27.5, -16) * mm});
            skLineSegment(sketch, "E18.3.2.24", {"start": v(12.5, -18) * mm, "end": v(12.5, -16) * mm});
            skLineSegment(sketch, "E18.3.2.25", {"start": v(27.5, -26.5) * mm, "end": v(27.5, -28.5) * mm});
            skLineSegment(sketch, "E18.3.2.26", {"start": v(12.5, -22) * mm, "end": v(12.5, -24) * mm});
            skLineSegment(sketch, "E18.4.0.0", {"start": v(7.5, 11.5) * mm, "end": v(-7.5, 11.5) * mm});
            skLineSegment(sketch, "E18.4.0.1", {"start": v(7.5, 28.5) * mm, "end": v(-7.5, 28.5) * mm});
            skLineSegment(sketch, "E18.4.0.2", {"start": v(7.5, 16) * mm, "end": v(-7.5, 16) * mm});
            skLineSegment(sketch, "E18.4.0.3", {"start": v(9.5, 10.5) * mm, "end": v(-9.5, 10.5) * mm, "construction": true});
            skPoint(sketch, "E18.4.0.4", {"position": v(0, 17) * mm});
            skLineSegment(sketch, "E18.4.0.5", {"start": v(9.5, 29.5) * mm, "end": v(-9.5, 29.5) * mm, "construction": true});
            skLineSegment(sketch, "E18.4.0.6", {"start": v(7.5, 26.5) * mm, "end": v(-7.5, 26.5) * mm});
            skLineSegment(sketch, "E18.4.0.7", {"start": v(9.5, 10.5) * mm, "end": v(9.5, 29.5) * mm, "construction": true});
            skPoint(sketch, "E18.4.0.8", {"position": v(0, 23) * mm});
            skLineSegment(sketch, "E18.4.0.9", {"start": v(7.5, 13.5) * mm, "end": v(-7.5, 13.5) * mm});
            skLineSegment(sketch, "E18.4.0.10", {"start": v(7.5, 24) * mm, "end": v(-7.5, 24) * mm});
            skLineSegment(sketch, "E18.4.0.11", {"start": v(7.5, 18) * mm, "end": v(-7.5, 18) * mm});
            skPoint(sketch, "E18.4.0.12", {"position": v(0, 27.5) * mm});
            skLineSegment(sketch, "E18.4.0.13", {"start": v(-9.5, 10.5) * mm, "end": v(-9.5, 29.5) * mm, "construction": true});
            skPoint(sketch, "E18.4.0.14", {"position": v(0, 12.5) * mm});
            skLineSegment(sketch, "E18.4.0.15", {"start": v(7.5, 22) * mm, "end": v(-7.5, 22) * mm});
            skCircle(sketch, "E18.4.0.16", {"center": v(-5.5, 20) * mm, "radius": 1 * mm});
            skCircle(sketch, "E18.4.0.17", {"center": v(5.5, 20) * mm, "radius": 1 * mm});
            skPoint(sketch, "E18.4.0.18", {"position": v(0, 20) * mm});
            skLineSegment(sketch, "E18.4.0.19", {"start": v(-7.5, 13.5) * mm, "end": v(-7.5, 11.5) * mm});
            skLineSegment(sketch, "E18.4.0.20", {"start": v(7.5, 26.5) * mm, "end": v(7.5, 28.5) * mm});
            skLineSegment(sketch, "E18.4.0.21", {"start": v(-7.5, 26.5) * mm, "end": v(-7.5, 28.5) * mm});
            skLineSegment(sketch, "E18.4.0.22", {"start": v(7.5, 18) * mm, "end": v(7.5, 16) * mm});
            skLineSegment(sketch, "E18.4.0.23", {"start": v(7.5, 22) * mm, "end": v(7.5, 24) * mm});
            skLineSegment(sketch, "E18.4.0.24", {"start": v(-7.5, 22) * mm, "end": v(-7.5, 24) * mm});
            skLineSegment(sketch, "E18.4.0.25", {"start": v(7.5, 13.5) * mm, "end": v(7.5, 11.5) * mm});
            skLineSegment(sketch, "E18.4.0.26", {"start": v(-7.5, 18) * mm, "end": v(-7.5, 16) * mm});
            skLineSegment(sketch, "E18.4.1.0", {"start": v(7.5, -8.5) * mm, "end": v(-7.5, -8.5) * mm});
            skLineSegment(sketch, "E18.4.1.1", {"start": v(7.5, 8.5) * mm, "end": v(-7.5, 8.5) * mm});
            skLineSegment(sketch, "E18.4.1.2", {"start": v(7.5, -4) * mm, "end": v(-7.5, -4) * mm});
            skLineSegment(sketch, "E18.4.1.3", {"start": v(9.5, -9.5) * mm, "end": v(-9.5, -9.5) * mm, "construction": true});
            skPoint(sketch, "E18.4.1.4", {"position": v(0, -3) * mm});
            skLineSegment(sketch, "E18.4.1.5", {"start": v(9.5, 9.5) * mm, "end": v(-9.5, 9.5) * mm, "construction": true});
            skLineSegment(sketch, "E18.4.1.6", {"start": v(7.5, 6.5) * mm, "end": v(-7.5, 6.5) * mm});
            skLineSegment(sketch, "E18.4.1.7", {"start": v(9.5, -9.5) * mm, "end": v(9.5, 9.5) * mm, "construction": true});
            skPoint(sketch, "E18.4.1.8", {"position": v(0, 3) * mm});
            skLineSegment(sketch, "E18.4.1.9", {"start": v(7.5, -6.5) * mm, "end": v(-7.5, -6.5) * mm});
            skLineSegment(sketch, "E18.4.1.10", {"start": v(7.5, 4) * mm, "end": v(-7.5, 4) * mm});
            skLineSegment(sketch, "E18.4.1.11", {"start": v(7.5, -2) * mm, "end": v(-7.5, -2) * mm});
            skPoint(sketch, "E18.4.1.12", {"position": v(0, 7.5) * mm});
            skLineSegment(sketch, "E18.4.1.13", {"start": v(-9.5, -9.5) * mm, "end": v(-9.5, 9.5) * mm, "construction": true});
            skPoint(sketch, "E18.4.1.14", {"position": v(0, -7.5) * mm});
            skLineSegment(sketch, "E18.4.1.15", {"start": v(7.5, 2) * mm, "end": v(-7.5, 2) * mm});
            skCircle(sketch, "E18.4.1.16", {"center": v(-5.5, 0) * mm, "radius": 1 * mm});
            skCircle(sketch, "E18.4.1.17", {"center": v(5.5, 0) * mm, "radius": 1 * mm});
            skPoint(sketch, "E18.4.1.18", {"position": v(0, 0) * mm});
            skLineSegment(sketch, "E18.4.1.19", {"start": v(-7.5, -6.5) * mm, "end": v(-7.5, -8.5) * mm});
            skLineSegment(sketch, "E18.4.1.20", {"start": v(7.5, 6.5) * mm, "end": v(7.5, 8.5) * mm});
            skLineSegment(sketch, "E18.4.1.21", {"start": v(-7.5, 6.5) * mm, "end": v(-7.5, 8.5) * mm});
            skLineSegment(sketch, "E18.4.1.22", {"start": v(7.5, -2) * mm, "end": v(7.5, -4) * mm});
            skLineSegment(sketch, "E18.4.1.23", {"start": v(7.5, 2) * mm, "end": v(7.5, 4) * mm});
            skLineSegment(sketch, "E18.4.1.24", {"start": v(-7.5, 2) * mm, "end": v(-7.5, 4) * mm});
            skLineSegment(sketch, "E18.4.1.25", {"start": v(7.5, -6.5) * mm, "end": v(7.5, -8.5) * mm});
            skLineSegment(sketch, "E18.4.1.26", {"start": v(-7.5, -2) * mm, "end": v(-7.5, -4) * mm});
            skLineSegment(sketch, "E18.4.2.0", {"start": v(7.5, -28.5) * mm, "end": v(-7.5, -28.5) * mm});
            skLineSegment(sketch, "E18.4.2.1", {"start": v(7.5, -11.5) * mm, "end": v(-7.5, -11.5) * mm});
            skLineSegment(sketch, "E18.4.2.2", {"start": v(7.5, -24) * mm, "end": v(-7.5, -24) * mm});
            skLineSegment(sketch, "E18.4.2.3", {"start": v(9.5, -29.5) * mm, "end": v(-9.5, -29.5) * mm, "construction": true});
            skPoint(sketch, "E18.4.2.4", {"position": v(0, -23) * mm});
            skLineSegment(sketch, "E18.4.2.5", {"start": v(9.5, -10.5) * mm, "end": v(-9.5, -10.5) * mm, "construction": true});
            skLineSegment(sketch, "E18.4.2.6", {"start": v(7.5, -13.5) * mm, "end": v(-7.5, -13.5) * mm});
            skLineSegment(sketch, "E18.4.2.7", {"start": v(9.5, -29.5) * mm, "end": v(9.5, -10.5) * mm, "construction": true});
            skPoint(sketch, "E18.4.2.8", {"position": v(0, -17) * mm});
            skLineSegment(sketch, "E18.4.2.9", {"start": v(7.5, -26.5) * mm, "end": v(-7.5, -26.5) * mm});
            skLineSegment(sketch, "E18.4.2.10", {"start": v(7.5, -16) * mm, "end": v(-7.5, -16) * mm});
            skLineSegment(sketch, "E18.4.2.11", {"start": v(7.5, -22) * mm, "end": v(-7.5, -22) * mm});
            skPoint(sketch, "E18.4.2.12", {"position": v(0, -12.5) * mm});
            skLineSegment(sketch, "E18.4.2.13", {"start": v(-9.5, -29.5) * mm, "end": v(-9.5, -10.5) * mm, "construction": true});
            skPoint(sketch, "E18.4.2.14", {"position": v(0, -27.5) * mm});
            skLineSegment(sketch, "E18.4.2.15", {"start": v(7.5, -18) * mm, "end": v(-7.5, -18) * mm});
            skCircle(sketch, "E18.4.2.16", {"center": v(-5.5, -20) * mm, "radius": 1 * mm});
            skCircle(sketch, "E18.4.2.17", {"center": v(5.5, -20) * mm, "radius": 1 * mm});
            skPoint(sketch, "E18.4.2.18", {"position": v(0, -20) * mm});
            skLineSegment(sketch, "E18.4.2.19", {"start": v(-7.5, -26.5) * mm, "end": v(-7.5, -28.5) * mm});
            skLineSegment(sketch, "E18.4.2.20", {"start": v(7.5, -13.5) * mm, "end": v(7.5, -11.5) * mm});
            skLineSegment(sketch, "E18.4.2.21", {"start": v(-7.5, -13.5) * mm, "end": v(-7.5, -11.5) * mm});
            skLineSegment(sketch, "E18.4.2.22", {"start": v(7.5, -22) * mm, "end": v(7.5, -24) * mm});
            skLineSegment(sketch, "E18.4.2.23", {"start": v(7.5, -18) * mm, "end": v(7.5, -16) * mm});
            skLineSegment(sketch, "E18.4.2.24", {"start": v(-7.5, -18) * mm, "end": v(-7.5, -16) * mm});
            skLineSegment(sketch, "E18.4.2.25", {"start": v(7.5, -26.5) * mm, "end": v(7.5, -28.5) * mm});
            skLineSegment(sketch, "E18.4.2.26", {"start": v(-7.5, -22) * mm, "end": v(-7.5, -24) * mm});
            skLineSegment(sketch, "E18.5.0.0", {"start": v(-12.5, 11.5) * mm, "end": v(-27.5, 11.5) * mm});
            skLineSegment(sketch, "E18.5.0.1", {"start": v(-12.5, 28.5) * mm, "end": v(-27.5, 28.5) * mm});
            skLineSegment(sketch, "E18.5.0.2", {"start": v(-12.5, 16) * mm, "end": v(-27.5, 16) * mm});
            skLineSegment(sketch, "E18.5.0.3", {"start": v(-10.5, 10.5) * mm, "end": v(-29.5, 10.5) * mm, "construction": true});
            skPoint(sketch, "E18.5.0.4", {"position": v(-20, 17) * mm});
            skLineSegment(sketch, "E18.5.0.5", {"start": v(-10.5, 29.5) * mm, "end": v(-29.5, 29.5) * mm, "construction": true});
            skLineSegment(sketch, "E18.5.0.6", {"start": v(-12.5, 26.5) * mm, "end": v(-27.5, 26.5) * mm});
            skLineSegment(sketch, "E18.5.0.7", {"start": v(-10.5, 10.5) * mm, "end": v(-10.5, 29.5) * mm, "construction": true});
            skPoint(sketch, "E18.5.0.8", {"position": v(-20, 23) * mm});
            skLineSegment(sketch, "E18.5.0.9", {"start": v(-12.5, 13.5) * mm, "end": v(-27.5, 13.5) * mm});
            skLineSegment(sketch, "E18.5.0.10", {"start": v(-12.5, 24) * mm, "end": v(-27.5, 24) * mm});
            skLineSegment(sketch, "E18.5.0.11", {"start": v(-12.5, 18) * mm, "end": v(-27.5, 18) * mm});
            skPoint(sketch, "E18.5.0.12", {"position": v(-20, 27.5) * mm});
            skLineSegment(sketch, "E18.5.0.13", {"start": v(-29.5, 10.5) * mm, "end": v(-29.5, 29.5) * mm, "construction": true});
            skPoint(sketch, "E18.5.0.14", {"position": v(-20, 12.5) * mm});
            skLineSegment(sketch, "E18.5.0.15", {"start": v(-12.5, 22) * mm, "end": v(-27.5, 22) * mm});
            skCircle(sketch, "E18.5.0.16", {"center": v(-25.5, 20) * mm, "radius": 1 * mm});
            skCircle(sketch, "E18.5.0.17", {"center": v(-14.5, 20) * mm, "radius": 1 * mm});
            skPoint(sketch, "E18.5.0.18", {"position": v(-20, 20) * mm});
            skLineSegment(sketch, "E18.5.0.19", {"start": v(-27.5, 13.5) * mm, "end": v(-27.5, 11.5) * mm});
            skLineSegment(sketch, "E18.5.0.20", {"start": v(-12.5, 26.5) * mm, "end": v(-12.5, 28.5) * mm});
            skLineSegment(sketch, "E18.5.0.21", {"start": v(-27.5, 26.5) * mm, "end": v(-27.5, 28.5) * mm});
            skLineSegment(sketch, "E18.5.0.22", {"start": v(-12.5, 18) * mm, "end": v(-12.5, 16) * mm});
            skLineSegment(sketch, "E18.5.0.23", {"start": v(-12.5, 22) * mm, "end": v(-12.5, 24) * mm});
            skLineSegment(sketch, "E18.5.0.24", {"start": v(-27.5, 22) * mm, "end": v(-27.5, 24) * mm});
            skLineSegment(sketch, "E18.5.0.25", {"start": v(-12.5, 13.5) * mm, "end": v(-12.5, 11.5) * mm});
            skLineSegment(sketch, "E18.5.0.26", {"start": v(-27.5, 18) * mm, "end": v(-27.5, 16) * mm});
            skLineSegment(sketch, "E18.5.1.0", {"start": v(-12.5, -8.5) * mm, "end": v(-27.5, -8.5) * mm});
            skLineSegment(sketch, "E18.5.1.1", {"start": v(-12.5, 8.5) * mm, "end": v(-27.5, 8.5) * mm});
            skLineSegment(sketch, "E18.5.1.2", {"start": v(-12.5, -4) * mm, "end": v(-27.5, -4) * mm});
            skLineSegment(sketch, "E18.5.1.3", {"start": v(-10.5, -9.5) * mm, "end": v(-29.5, -9.5) * mm, "construction": true});
            skPoint(sketch, "E18.5.1.4", {"position": v(-20, -3) * mm});
            skLineSegment(sketch, "E18.5.1.5", {"start": v(-10.5, 9.5) * mm, "end": v(-29.5, 9.5) * mm, "construction": true});
            skLineSegment(sketch, "E18.5.1.6", {"start": v(-12.5, 6.5) * mm, "end": v(-27.5, 6.5) * mm});
            skLineSegment(sketch, "E18.5.1.7", {"start": v(-10.5, -9.5) * mm, "end": v(-10.5, 9.5) * mm, "construction": true});
            skPoint(sketch, "E18.5.1.8", {"position": v(-20, 3) * mm});
            skLineSegment(sketch, "E18.5.1.9", {"start": v(-12.5, -6.5) * mm, "end": v(-27.5, -6.5) * mm});
            skLineSegment(sketch, "E18.5.1.10", {"start": v(-12.5, 4) * mm, "end": v(-27.5, 4) * mm});
            skLineSegment(sketch, "E18.5.1.11", {"start": v(-12.5, -2) * mm, "end": v(-27.5, -2) * mm});
            skPoint(sketch, "E18.5.1.12", {"position": v(-20, 7.5) * mm});
            skLineSegment(sketch, "E18.5.1.13", {"start": v(-29.5, -9.5) * mm, "end": v(-29.5, 9.5) * mm, "construction": true});
            skPoint(sketch, "E18.5.1.14", {"position": v(-20, -7.5) * mm});
            skLineSegment(sketch, "E18.5.1.15", {"start": v(-12.5, 2) * mm, "end": v(-27.5, 2) * mm});
            skCircle(sketch, "E18.5.1.16", {"center": v(-25.5, 0) * mm, "radius": 1 * mm});
            skCircle(sketch, "E18.5.1.17", {"center": v(-14.5, 0) * mm, "radius": 1 * mm});
            skPoint(sketch, "E18.5.1.18", {"position": v(-20, 0) * mm});
            skLineSegment(sketch, "E18.5.1.19", {"start": v(-27.5, -6.5) * mm, "end": v(-27.5, -8.5) * mm});
            skLineSegment(sketch, "E18.5.1.20", {"start": v(-12.5, 6.5) * mm, "end": v(-12.5, 8.5) * mm});
            skLineSegment(sketch, "E18.5.1.21", {"start": v(-27.5, 6.5) * mm, "end": v(-27.5, 8.5) * mm});
            skLineSegment(sketch, "E18.5.1.22", {"start": v(-12.5, -2) * mm, "end": v(-12.5, -4) * mm});
            skLineSegment(sketch, "E18.5.1.23", {"start": v(-12.5, 2) * mm, "end": v(-12.5, 4) * mm});
            skLineSegment(sketch, "E18.5.1.24", {"start": v(-27.5, 2) * mm, "end": v(-27.5, 4) * mm});
            skLineSegment(sketch, "E18.5.1.25", {"start": v(-12.5, -6.5) * mm, "end": v(-12.5, -8.5) * mm});
            skLineSegment(sketch, "E18.5.1.26", {"start": v(-27.5, -2) * mm, "end": v(-27.5, -4) * mm});
            skLineSegment(sketch, "E18.5.2.0", {"start": v(-12.5, -28.5) * mm, "end": v(-27.5, -28.5) * mm});
            skLineSegment(sketch, "E18.5.2.1", {"start": v(-12.5, -11.5) * mm, "end": v(-27.5, -11.5) * mm});
            skLineSegment(sketch, "E18.5.2.2", {"start": v(-12.5, -24) * mm, "end": v(-27.5, -24) * mm});
            skLineSegment(sketch, "E18.5.2.3", {"start": v(-10.5, -29.5) * mm, "end": v(-29.5, -29.5) * mm, "construction": true});
            skPoint(sketch, "E18.5.2.4", {"position": v(-20, -23) * mm});
            skLineSegment(sketch, "E18.5.2.5", {"start": v(-10.5, -10.5) * mm, "end": v(-29.5, -10.5) * mm, "construction": true});
            skLineSegment(sketch, "E18.5.2.6", {"start": v(-12.5, -13.5) * mm, "end": v(-27.5, -13.5) * mm});
            skLineSegment(sketch, "E18.5.2.7", {"start": v(-10.5, -29.5) * mm, "end": v(-10.5, -10.5) * mm, "construction": true});
            skPoint(sketch, "E18.5.2.8", {"position": v(-20, -17) * mm});
            skLineSegment(sketch, "E18.5.2.9", {"start": v(-12.5, -26.5) * mm, "end": v(-27.5, -26.5) * mm});
            skLineSegment(sketch, "E18.5.2.10", {"start": v(-12.5, -16) * mm, "end": v(-27.5, -16) * mm});
            skLineSegment(sketch, "E18.5.2.11", {"start": v(-12.5, -22) * mm, "end": v(-27.5, -22) * mm});
            skPoint(sketch, "E18.5.2.12", {"position": v(-20, -12.5) * mm});
            skLineSegment(sketch, "E18.5.2.13", {"start": v(-29.5, -29.5) * mm, "end": v(-29.5, -10.5) * mm, "construction": true});
            skPoint(sketch, "E18.5.2.14", {"position": v(-20, -27.5) * mm});
            skLineSegment(sketch, "E18.5.2.15", {"start": v(-12.5, -18) * mm, "end": v(-27.5, -18) * mm});
            skCircle(sketch, "E18.5.2.16", {"center": v(-25.5, -20) * mm, "radius": 1 * mm});
            skCircle(sketch, "E18.5.2.17", {"center": v(-14.5, -20) * mm, "radius": 1 * mm});
            skPoint(sketch, "E18.5.2.18", {"position": v(-20, -20) * mm});
            skLineSegment(sketch, "E18.5.2.19", {"start": v(-27.5, -26.5) * mm, "end": v(-27.5, -28.5) * mm});
            skLineSegment(sketch, "E18.5.2.20", {"start": v(-12.5, -13.5) * mm, "end": v(-12.5, -11.5) * mm});
            skLineSegment(sketch, "E18.5.2.21", {"start": v(-27.5, -13.5) * mm, "end": v(-27.5, -11.5) * mm});
            skLineSegment(sketch, "E18.5.2.22", {"start": v(-12.5, -22) * mm, "end": v(-12.5, -24) * mm});
            skLineSegment(sketch, "E18.5.2.23", {"start": v(-12.5, -18) * mm, "end": v(-12.5, -16) * mm});
            skLineSegment(sketch, "E18.5.2.24", {"start": v(-27.5, -18) * mm, "end": v(-27.5, -16) * mm});
            skLineSegment(sketch, "E18.5.2.25", {"start": v(-12.5, -26.5) * mm, "end": v(-12.5, -28.5) * mm});
            skLineSegment(sketch, "E18.5.2.26", {"start": v(-27.5, -22) * mm, "end": v(-27.5, -24) * mm});
            skLineSegment(sketch, "E18.6.0.0", {"start": v(-32.5, 11.5) * mm, "end": v(-47.5, 11.5) * mm});
            skLineSegment(sketch, "E18.6.0.1", {"start": v(-32.5, 28.5) * mm, "end": v(-47.5, 28.5) * mm});
            skLineSegment(sketch, "E18.6.0.2", {"start": v(-32.5, 16) * mm, "end": v(-47.5, 16) * mm});
            skLineSegment(sketch, "E18.6.0.3", {"start": v(-30.5, 10.5) * mm, "end": v(-49.5, 10.5) * mm, "construction": true});
            skPoint(sketch, "E18.6.0.4", {"position": v(-40, 17) * mm});
            skLineSegment(sketch, "E18.6.0.5", {"start": v(-30.5, 29.5) * mm, "end": v(-49.5, 29.5) * mm, "construction": true});
            skLineSegment(sketch, "E18.6.0.6", {"start": v(-32.5, 26.5) * mm, "end": v(-47.5, 26.5) * mm});
            skLineSegment(sketch, "E18.6.0.7", {"start": v(-30.5, 10.5) * mm, "end": v(-30.5, 29.5) * mm, "construction": true});
            skPoint(sketch, "E18.6.0.8", {"position": v(-40, 23) * mm});
            skLineSegment(sketch, "E18.6.0.9", {"start": v(-32.5, 13.5) * mm, "end": v(-47.5, 13.5) * mm});
            skLineSegment(sketch, "E18.6.0.10", {"start": v(-32.5, 24) * mm, "end": v(-47.5, 24) * mm});
            skLineSegment(sketch, "E18.6.0.11", {"start": v(-32.5, 18) * mm, "end": v(-47.5, 18) * mm});
            skPoint(sketch, "E18.6.0.12", {"position": v(-40, 27.5) * mm});
            skLineSegment(sketch, "E18.6.0.13", {"start": v(-49.5, 10.5) * mm, "end": v(-49.5, 29.5) * mm, "construction": true});
            skPoint(sketch, "E18.6.0.14", {"position": v(-40, 12.5) * mm});
            skLineSegment(sketch, "E18.6.0.15", {"start": v(-32.5, 22) * mm, "end": v(-47.5, 22) * mm});
            skCircle(sketch, "E18.6.0.16", {"center": v(-45.5, 20) * mm, "radius": 1 * mm});
            skCircle(sketch, "E18.6.0.17", {"center": v(-34.5, 20) * mm, "radius": 1 * mm});
            skPoint(sketch, "E18.6.0.18", {"position": v(-40, 20) * mm});
            skLineSegment(sketch, "E18.6.0.19", {"start": v(-47.5, 13.5) * mm, "end": v(-47.5, 11.5) * mm});
            skLineSegment(sketch, "E18.6.0.20", {"start": v(-32.5, 26.5) * mm, "end": v(-32.5, 28.5) * mm});
            skLineSegment(sketch, "E18.6.0.21", {"start": v(-47.5, 26.5) * mm, "end": v(-47.5, 28.5) * mm});
            skLineSegment(sketch, "E18.6.0.22", {"start": v(-32.5, 18) * mm, "end": v(-32.5, 16) * mm});
            skLineSegment(sketch, "E18.6.0.23", {"start": v(-32.5, 22) * mm, "end": v(-32.5, 24) * mm});
            skLineSegment(sketch, "E18.6.0.24", {"start": v(-47.5, 22) * mm, "end": v(-47.5, 24) * mm});
            skLineSegment(sketch, "E18.6.0.25", {"start": v(-32.5, 13.5) * mm, "end": v(-32.5, 11.5) * mm});
            skLineSegment(sketch, "E18.6.0.26", {"start": v(-47.5, 18) * mm, "end": v(-47.5, 16) * mm});
            skLineSegment(sketch, "E18.6.1.0", {"start": v(-32.5, -8.5) * mm, "end": v(-47.5, -8.5) * mm});
            skLineSegment(sketch, "E18.6.1.1", {"start": v(-32.5, 8.5) * mm, "end": v(-47.5, 8.5) * mm});
            skLineSegment(sketch, "E18.6.1.2", {"start": v(-32.5, -4) * mm, "end": v(-47.5, -4) * mm});
            skLineSegment(sketch, "E18.6.1.3", {"start": v(-30.5, -9.5) * mm, "end": v(-49.5, -9.5) * mm, "construction": true});
            skPoint(sketch, "E18.6.1.4", {"position": v(-40, -3) * mm});
            skLineSegment(sketch, "E18.6.1.5", {"start": v(-30.5, 9.5) * mm, "end": v(-49.5, 9.5) * mm, "construction": true});
            skLineSegment(sketch, "E18.6.1.6", {"start": v(-32.5, 6.5) * mm, "end": v(-47.5, 6.5) * mm});
            skLineSegment(sketch, "E18.6.1.7", {"start": v(-30.5, -9.5) * mm, "end": v(-30.5, 9.5) * mm, "construction": true});
            skPoint(sketch, "E18.6.1.8", {"position": v(-40, 3) * mm});
            skLineSegment(sketch, "E18.6.1.9", {"start": v(-32.5, -6.5) * mm, "end": v(-47.5, -6.5) * mm});
            skLineSegment(sketch, "E18.6.1.10", {"start": v(-32.5, 4) * mm, "end": v(-47.5, 4) * mm});
            skLineSegment(sketch, "E18.6.1.11", {"start": v(-32.5, -2) * mm, "end": v(-47.5, -2) * mm});
            skPoint(sketch, "E18.6.1.12", {"position": v(-40, 7.5) * mm});
            skLineSegment(sketch, "E18.6.1.13", {"start": v(-49.5, -9.5) * mm, "end": v(-49.5, 9.5) * mm, "construction": true});
            skPoint(sketch, "E18.6.1.14", {"position": v(-40, -7.5) * mm});
            skLineSegment(sketch, "E18.6.1.15", {"start": v(-32.5, 2) * mm, "end": v(-47.5, 2) * mm});
            skCircle(sketch, "E18.6.1.16", {"center": v(-45.5, 0) * mm, "radius": 1 * mm});
            skCircle(sketch, "E18.6.1.17", {"center": v(-34.5, 0) * mm, "radius": 1 * mm});
            skPoint(sketch, "E18.6.1.18", {"position": v(-40, 0) * mm});
            skLineSegment(sketch, "E18.6.1.19", {"start": v(-47.5, -6.5) * mm, "end": v(-47.5, -8.5) * mm});
            skLineSegment(sketch, "E18.6.1.20", {"start": v(-32.5, 6.5) * mm, "end": v(-32.5, 8.5) * mm});
            skLineSegment(sketch, "E18.6.1.21", {"start": v(-47.5, 6.5) * mm, "end": v(-47.5, 8.5) * mm});
            skLineSegment(sketch, "E18.6.1.22", {"start": v(-32.5, -2) * mm, "end": v(-32.5, -4) * mm});
            skLineSegment(sketch, "E18.6.1.23", {"start": v(-32.5, 2) * mm, "end": v(-32.5, 4) * mm});
            skLineSegment(sketch, "E18.6.1.24", {"start": v(-47.5, 2) * mm, "end": v(-47.5, 4) * mm});
            skLineSegment(sketch, "E18.6.1.25", {"start": v(-32.5, -6.5) * mm, "end": v(-32.5, -8.5) * mm});
            skLineSegment(sketch, "E18.6.1.26", {"start": v(-47.5, -2) * mm, "end": v(-47.5, -4) * mm});
            skLineSegment(sketch, "E18.6.2.0", {"start": v(-32.5, -28.5) * mm, "end": v(-47.5, -28.5) * mm});
            skLineSegment(sketch, "E18.6.2.1", {"start": v(-32.5, -11.5) * mm, "end": v(-47.5, -11.5) * mm});
            skLineSegment(sketch, "E18.6.2.2", {"start": v(-32.5, -24) * mm, "end": v(-47.5, -24) * mm});
            skLineSegment(sketch, "E18.6.2.3", {"start": v(-30.5, -29.5) * mm, "end": v(-49.5, -29.5) * mm, "construction": true});
            skPoint(sketch, "E18.6.2.4", {"position": v(-40, -23) * mm});
            skLineSegment(sketch, "E18.6.2.5", {"start": v(-30.5, -10.5) * mm, "end": v(-49.5, -10.5) * mm, "construction": true});
            skLineSegment(sketch, "E18.6.2.6", {"start": v(-32.5, -13.5) * mm, "end": v(-47.5, -13.5) * mm});
            skLineSegment(sketch, "E18.6.2.7", {"start": v(-30.5, -29.5) * mm, "end": v(-30.5, -10.5) * mm, "construction": true});
            skPoint(sketch, "E18.6.2.8", {"position": v(-40, -17) * mm});
            skLineSegment(sketch, "E18.6.2.9", {"start": v(-32.5, -26.5) * mm, "end": v(-47.5, -26.5) * mm});
            skLineSegment(sketch, "E18.6.2.10", {"start": v(-32.5, -16) * mm, "end": v(-47.5, -16) * mm});
            skLineSegment(sketch, "E18.6.2.11", {"start": v(-32.5, -22) * mm, "end": v(-47.5, -22) * mm});
            skPoint(sketch, "E18.6.2.12", {"position": v(-40, -12.5) * mm});
            skLineSegment(sketch, "E18.6.2.13", {"start": v(-49.5, -29.5) * mm, "end": v(-49.5, -10.5) * mm, "construction": true});
            skPoint(sketch, "E18.6.2.14", {"position": v(-40, -27.5) * mm});
            skLineSegment(sketch, "E18.6.2.15", {"start": v(-32.5, -18) * mm, "end": v(-47.5, -18) * mm});
            skCircle(sketch, "E18.6.2.16", {"center": v(-45.5, -20) * mm, "radius": 1 * mm});
            skCircle(sketch, "E18.6.2.17", {"center": v(-34.5, -20) * mm, "radius": 1 * mm});
            skPoint(sketch, "E18.6.2.18", {"position": v(-40, -20) * mm});
            skLineSegment(sketch, "E18.6.2.19", {"start": v(-47.5, -26.5) * mm, "end": v(-47.5, -28.5) * mm});
            skLineSegment(sketch, "E18.6.2.20", {"start": v(-32.5, -13.5) * mm, "end": v(-32.5, -11.5) * mm});
            skLineSegment(sketch, "E18.6.2.21", {"start": v(-47.5, -13.5) * mm, "end": v(-47.5, -11.5) * mm});
            skLineSegment(sketch, "E18.6.2.22", {"start": v(-32.5, -22) * mm, "end": v(-32.5, -24) * mm});
            skLineSegment(sketch, "E18.6.2.23", {"start": v(-32.5, -18) * mm, "end": v(-32.5, -16) * mm});
            skLineSegment(sketch, "E18.6.2.24", {"start": v(-47.5, -18) * mm, "end": v(-47.5, -16) * mm});
            skLineSegment(sketch, "E18.6.2.25", {"start": v(-32.5, -26.5) * mm, "end": v(-32.5, -28.5) * mm});
            skLineSegment(sketch, "E18.6.2.26", {"start": v(-47.5, -22) * mm, "end": v(-47.5, -24) * mm});
            skLineSegment(sketch, "E18.7.0.0", {"start": v(-52.5, 11.5) * mm, "end": v(-67.5, 11.5) * mm});
            skLineSegment(sketch, "E18.7.0.1", {"start": v(-52.5, 28.5) * mm, "end": v(-67.5, 28.5) * mm});
            skLineSegment(sketch, "E18.7.0.2", {"start": v(-52.5, 16) * mm, "end": v(-67.5, 16) * mm});
            skLineSegment(sketch, "E18.7.0.3", {"start": v(-50.5, 10.5) * mm, "end": v(-69.5, 10.5) * mm, "construction": true});
            skPoint(sketch, "E18.7.0.4", {"position": v(-60, 17) * mm});
            skLineSegment(sketch, "E18.7.0.5", {"start": v(-50.5, 29.5) * mm, "end": v(-69.5, 29.5) * mm, "construction": true});
            skLineSegment(sketch, "E18.7.0.6", {"start": v(-52.5, 26.5) * mm, "end": v(-67.5, 26.5) * mm});
            skLineSegment(sketch, "E18.7.0.7", {"start": v(-50.5, 10.5) * mm, "end": v(-50.5, 29.5) * mm, "construction": true});
            skPoint(sketch, "E18.7.0.8", {"position": v(-60, 23) * mm});
            skLineSegment(sketch, "E18.7.0.9", {"start": v(-52.5, 13.5) * mm, "end": v(-67.5, 13.5) * mm});
            skLineSegment(sketch, "E18.7.0.10", {"start": v(-52.5, 24) * mm, "end": v(-67.5, 24) * mm});
            skLineSegment(sketch, "E18.7.0.11", {"start": v(-52.5, 18) * mm, "end": v(-67.5, 18) * mm});
            skPoint(sketch, "E18.7.0.12", {"position": v(-60, 27.5) * mm});
            skLineSegment(sketch, "E18.7.0.13", {"start": v(-69.5, 10.5) * mm, "end": v(-69.5, 29.5) * mm, "construction": true});
            skPoint(sketch, "E18.7.0.14", {"position": v(-60, 12.5) * mm});
            skLineSegment(sketch, "E18.7.0.15", {"start": v(-52.5, 22) * mm, "end": v(-67.5, 22) * mm});
            skCircle(sketch, "E18.7.0.16", {"center": v(-65.5, 20) * mm, "radius": 1 * mm});
            skCircle(sketch, "E18.7.0.17", {"center": v(-54.5, 20) * mm, "radius": 1 * mm});
            skPoint(sketch, "E18.7.0.18", {"position": v(-60, 20) * mm});
            skLineSegment(sketch, "E18.7.0.19", {"start": v(-67.5, 13.5) * mm, "end": v(-67.5, 11.5) * mm});
            skLineSegment(sketch, "E18.7.0.20", {"start": v(-52.5, 26.5) * mm, "end": v(-52.5, 28.5) * mm});
            skLineSegment(sketch, "E18.7.0.21", {"start": v(-67.5, 26.5) * mm, "end": v(-67.5, 28.5) * mm});
            skLineSegment(sketch, "E18.7.0.22", {"start": v(-52.5, 18) * mm, "end": v(-52.5, 16) * mm});
            skLineSegment(sketch, "E18.7.0.23", {"start": v(-52.5, 22) * mm, "end": v(-52.5, 24) * mm});
            skLineSegment(sketch, "E18.7.0.24", {"start": v(-67.5, 22) * mm, "end": v(-67.5, 24) * mm});
            skLineSegment(sketch, "E18.7.0.25", {"start": v(-52.5, 13.5) * mm, "end": v(-52.5, 11.5) * mm});
            skLineSegment(sketch, "E18.7.0.26", {"start": v(-67.5, 18) * mm, "end": v(-67.5, 16) * mm});
            skLineSegment(sketch, "E18.7.1.0", {"start": v(-52.5, -8.5) * mm, "end": v(-67.5, -8.5) * mm});
            skLineSegment(sketch, "E18.7.1.1", {"start": v(-52.5, 8.5) * mm, "end": v(-67.5, 8.5) * mm});
            skLineSegment(sketch, "E18.7.1.2", {"start": v(-52.5, -4) * mm, "end": v(-67.5, -4) * mm});
            skLineSegment(sketch, "E18.7.1.3", {"start": v(-50.5, -9.5) * mm, "end": v(-69.5, -9.5) * mm, "construction": true});
            skPoint(sketch, "E18.7.1.4", {"position": v(-60, -3) * mm});
            skLineSegment(sketch, "E18.7.1.5", {"start": v(-50.5, 9.5) * mm, "end": v(-69.5, 9.5) * mm, "construction": true});
            skLineSegment(sketch, "E18.7.1.6", {"start": v(-52.5, 6.5) * mm, "end": v(-67.5, 6.5) * mm});
            skLineSegment(sketch, "E18.7.1.7", {"start": v(-50.5, -9.5) * mm, "end": v(-50.5, 9.5) * mm, "construction": true});
            skPoint(sketch, "E18.7.1.8", {"position": v(-60, 3) * mm});
            skLineSegment(sketch, "E18.7.1.9", {"start": v(-52.5, -6.5) * mm, "end": v(-67.5, -6.5) * mm});
            skLineSegment(sketch, "E18.7.1.10", {"start": v(-52.5, 4) * mm, "end": v(-67.5, 4) * mm});
            skLineSegment(sketch, "E18.7.1.11", {"start": v(-52.5, -2) * mm, "end": v(-67.5, -2) * mm});
            skPoint(sketch, "E18.7.1.12", {"position": v(-60, 7.5) * mm});
            skLineSegment(sketch, "E18.7.1.13", {"start": v(-69.5, -9.5) * mm, "end": v(-69.5, 9.5) * mm, "construction": true});
            skPoint(sketch, "E18.7.1.14", {"position": v(-60, -7.5) * mm});
            skLineSegment(sketch, "E18.7.1.15", {"start": v(-52.5, 2) * mm, "end": v(-67.5, 2) * mm});
            skCircle(sketch, "E18.7.1.16", {"center": v(-65.5, 0) * mm, "radius": 1 * mm});
            skCircle(sketch, "E18.7.1.17", {"center": v(-54.5, 0) * mm, "radius": 1 * mm});
            skPoint(sketch, "E18.7.1.18", {"position": v(-60, 0) * mm});
            skLineSegment(sketch, "E18.7.1.19", {"start": v(-67.5, -6.5) * mm, "end": v(-67.5, -8.5) * mm});
            skLineSegment(sketch, "E18.7.1.20", {"start": v(-52.5, 6.5) * mm, "end": v(-52.5, 8.5) * mm});
            skLineSegment(sketch, "E18.7.1.21", {"start": v(-67.5, 6.5) * mm, "end": v(-67.5, 8.5) * mm});
            skLineSegment(sketch, "E18.7.1.22", {"start": v(-52.5, -2) * mm, "end": v(-52.5, -4) * mm});
            skLineSegment(sketch, "E18.7.1.23", {"start": v(-52.5, 2) * mm, "end": v(-52.5, 4) * mm});
            skLineSegment(sketch, "E18.7.1.24", {"start": v(-67.5, 2) * mm, "end": v(-67.5, 4) * mm});
            skLineSegment(sketch, "E18.7.1.25", {"start": v(-52.5, -6.5) * mm, "end": v(-52.5, -8.5) * mm});
            skLineSegment(sketch, "E18.7.1.26", {"start": v(-67.5, -2) * mm, "end": v(-67.5, -4) * mm});
            skLineSegment(sketch, "E18.7.2.0", {"start": v(-52.5, -28.5) * mm, "end": v(-67.5, -28.5) * mm});
            skLineSegment(sketch, "E18.7.2.1", {"start": v(-52.5, -11.5) * mm, "end": v(-67.5, -11.5) * mm});
            skLineSegment(sketch, "E18.7.2.2", {"start": v(-52.5, -24) * mm, "end": v(-67.5, -24) * mm});
            skLineSegment(sketch, "E18.7.2.3", {"start": v(-50.5, -29.5) * mm, "end": v(-69.5, -29.5) * mm, "construction": true});
            skPoint(sketch, "E18.7.2.4", {"position": v(-60, -23) * mm});
            skLineSegment(sketch, "E18.7.2.5", {"start": v(-50.5, -10.5) * mm, "end": v(-69.5, -10.5) * mm, "construction": true});
            skLineSegment(sketch, "E18.7.2.6", {"start": v(-52.5, -13.5) * mm, "end": v(-67.5, -13.5) * mm});
            skLineSegment(sketch, "E18.7.2.7", {"start": v(-50.5, -29.5) * mm, "end": v(-50.5, -10.5) * mm, "construction": true});
            skPoint(sketch, "E18.7.2.8", {"position": v(-60, -17) * mm});
            skLineSegment(sketch, "E18.7.2.9", {"start": v(-52.5, -26.5) * mm, "end": v(-67.5, -26.5) * mm});
            skLineSegment(sketch, "E18.7.2.10", {"start": v(-52.5, -16) * mm, "end": v(-67.5, -16) * mm});
            skLineSegment(sketch, "E18.7.2.11", {"start": v(-52.5, -22) * mm, "end": v(-67.5, -22) * mm});
            skPoint(sketch, "E18.7.2.12", {"position": v(-60, -12.5) * mm});
            skLineSegment(sketch, "E18.7.2.13", {"start": v(-69.5, -29.5) * mm, "end": v(-69.5, -10.5) * mm, "construction": true});
            skPoint(sketch, "E18.7.2.14", {"position": v(-60, -27.5) * mm});
            skLineSegment(sketch, "E18.7.2.15", {"start": v(-52.5, -18) * mm, "end": v(-67.5, -18) * mm});
            skCircle(sketch, "E18.7.2.16", {"center": v(-65.5, -20) * mm, "radius": 1 * mm});
            skCircle(sketch, "E18.7.2.17", {"center": v(-54.5, -20) * mm, "radius": 1 * mm});
            skPoint(sketch, "E18.7.2.18", {"position": v(-60, -20) * mm});
            skLineSegment(sketch, "E18.7.2.19", {"start": v(-67.5, -26.5) * mm, "end": v(-67.5, -28.5) * mm});
            skLineSegment(sketch, "E18.7.2.20", {"start": v(-52.5, -13.5) * mm, "end": v(-52.5, -11.5) * mm});
            skLineSegment(sketch, "E18.7.2.21", {"start": v(-67.5, -13.5) * mm, "end": v(-67.5, -11.5) * mm});
            skLineSegment(sketch, "E18.7.2.22", {"start": v(-52.5, -22) * mm, "end": v(-52.5, -24) * mm});
            skLineSegment(sketch, "E18.7.2.23", {"start": v(-52.5, -18) * mm, "end": v(-52.5, -16) * mm});
            skLineSegment(sketch, "E18.7.2.24", {"start": v(-67.5, -18) * mm, "end": v(-67.5, -16) * mm});
            skLineSegment(sketch, "E18.7.2.25", {"start": v(-52.5, -26.5) * mm, "end": v(-52.5, -28.5) * mm});
            skLineSegment(sketch, "E18.7.2.26", {"start": v(-67.5, -22) * mm, "end": v(-67.5, -24) * mm});
            skLineSegment(sketch, "E18.8.0.3", {"start": v(-70.5, 10.5) * mm, "end": v(-89.5, 10.5) * mm, "construction": true});
            skLineSegment(sketch, "E18.8.0.5", {"start": v(-70.5, 29.5) * mm, "end": v(-89.5, 29.5) * mm, "construction": true});
            skLineSegment(sketch, "E18.8.0.7", {"start": v(-70.5, 10.5) * mm, "end": v(-70.5, 29.5) * mm, "construction": true});
            skLineSegment(sketch, "E18.8.0.13", {"start": v(-89.5, 10.5) * mm, "end": v(-89.5, 29.5) * mm, "construction": true});
            skPoint(sketch, "E18.8.0.18", {"position": v(-80, 20) * mm});
            skLineSegment(sketch, "E18.8.1.0", {"start": v(-72.5, -8.5) * mm, "end": v(-87.5, -8.5) * mm});
            skLineSegment(sketch, "E18.8.1.1", {"start": v(-72.5, 8.5) * mm, "end": v(-87.5, 8.5) * mm});
            skLineSegment(sketch, "E18.8.1.2", {"start": v(-72.5, -4) * mm, "end": v(-87.5, -4) * mm});
            skLineSegment(sketch, "E18.8.1.3", {"start": v(-70.5, -9.5) * mm, "end": v(-89.5, -9.5) * mm, "construction": true});
            skPoint(sketch, "E18.8.1.4", {"position": v(-80, -3) * mm});
            skLineSegment(sketch, "E18.8.1.5", {"start": v(-70.5, 9.5) * mm, "end": v(-89.5, 9.5) * mm, "construction": true});
            skLineSegment(sketch, "E18.8.1.6", {"start": v(-72.5, 6.5) * mm, "end": v(-87.5, 6.5) * mm});
            skLineSegment(sketch, "E18.8.1.7", {"start": v(-70.5, -9.5) * mm, "end": v(-70.5, 9.5) * mm, "construction": true});
            skPoint(sketch, "E18.8.1.8", {"position": v(-80, 3) * mm});
            skLineSegment(sketch, "E18.8.1.9", {"start": v(-72.5, -6.5) * mm, "end": v(-87.5, -6.5) * mm});
            skLineSegment(sketch, "E18.8.1.10", {"start": v(-72.5, 4) * mm, "end": v(-87.5, 4) * mm});
            skLineSegment(sketch, "E18.8.1.11", {"start": v(-72.5, -2) * mm, "end": v(-87.5, -2) * mm});
            skPoint(sketch, "E18.8.1.12", {"position": v(-80, 7.5) * mm});
            skLineSegment(sketch, "E18.8.1.13", {"start": v(-89.5, -9.5) * mm, "end": v(-89.5, 9.5) * mm, "construction": true});
            skPoint(sketch, "E18.8.1.14", {"position": v(-80, -7.5) * mm});
            skLineSegment(sketch, "E18.8.1.15", {"start": v(-72.5, 2) * mm, "end": v(-87.5, 2) * mm});
            skCircle(sketch, "E18.8.1.16", {"center": v(-85.5, 0) * mm, "radius": 1 * mm});
            skCircle(sketch, "E18.8.1.17", {"center": v(-74.5, 0) * mm, "radius": 1 * mm});
            skPoint(sketch, "E18.8.1.18", {"position": v(-80, 0) * mm});
            skLineSegment(sketch, "E18.8.1.19", {"start": v(-87.5, -6.5) * mm, "end": v(-87.5, -8.5) * mm});
            skLineSegment(sketch, "E18.8.1.20", {"start": v(-72.5, 6.5) * mm, "end": v(-72.5, 8.5) * mm});
            skLineSegment(sketch, "E18.8.1.21", {"start": v(-87.5, 6.5) * mm, "end": v(-87.5, 8.5) * mm});
            skLineSegment(sketch, "E18.8.1.22", {"start": v(-72.5, -2) * mm, "end": v(-72.5, -4) * mm});
            skLineSegment(sketch, "E18.8.1.23", {"start": v(-72.5, 2) * mm, "end": v(-72.5, 4) * mm});
            skLineSegment(sketch, "E18.8.1.24", {"start": v(-87.5, 2) * mm, "end": v(-87.5, 4) * mm});
            skLineSegment(sketch, "E18.8.1.25", {"start": v(-72.5, -6.5) * mm, "end": v(-72.5, -8.5) * mm});
            skLineSegment(sketch, "E18.8.1.26", {"start": v(-87.5, -2) * mm, "end": v(-87.5, -4) * mm});
            skLineSegment(sketch, "E18.8.2.3", {"start": v(-70.5, -29.5) * mm, "end": v(-89.5, -29.5) * mm, "construction": true});
            skLineSegment(sketch, "E18.8.2.5", {"start": v(-70.5, -10.5) * mm, "end": v(-89.5, -10.5) * mm, "construction": true});
            skLineSegment(sketch, "E18.8.2.7", {"start": v(-70.5, -29.5) * mm, "end": v(-70.5, -10.5) * mm, "construction": true});
            skLineSegment(sketch, "E18.8.2.13", {"start": v(-89.5, -29.5) * mm, "end": v(-89.5, -10.5) * mm, "construction": true});
            skPoint(sketch, "E18.8.2.18", {"position": v(-80, -20) * mm});
            skLineSegment(sketch, "E18.direction1", {"start": v(70.5, 10.5) * mm, "end": v(50.5, 10.5) * mm, "construction": true});
            skLineSegment(sketch, "E18.direction2", {"start": v(70.5, 10.5) * mm, "end": v(70.5, -9.5) * mm, "construction": true});
            skCircle(sketch, "E19", {"center": v(-86, 20) * mm, "radius": 1 * mm});
            skCircle(sketch, "E20", {"center": v(-74, 20) * mm, "radius": 1 * mm});
            skLineSegment(sketch, "E21.bottom", {"start": v(-76.5, 21.5) * mm, "end": v(-83.5, 21.5) * mm});
            skLineSegment(sketch, "E21.top", {"start": v(-76.5, 23.5) * mm, "end": v(-83.5, 23.5) * mm});
            skLineSegment(sketch, "E21.left", {"start": v(-76.5, 21.5) * mm, "end": v(-76.5, 23.5) * mm});
            skLineSegment(sketch, "E21.right", {"start": v(-83.5, 21.5) * mm, "end": v(-83.5, 23.5) * mm});
            skPoint(sketch, "E21.middle", {"position": v(-80, 22.5) * mm});
            skLineSegment(sketch, "E22.bottom", {"start": v(-76.5, 18.5) * mm, "end": v(-83.5, 18.5) * mm});
            skLineSegment(sketch, "E22.top", {"start": v(-76.5, 16.5) * mm, "end": v(-83.5, 16.5) * mm});
            skLineSegment(sketch, "E22.left", {"start": v(-76.5, 18.5) * mm, "end": v(-76.5, 16.5) * mm});
            skLineSegment(sketch, "E22.right", {"start": v(-83.5, 18.5) * mm, "end": v(-83.5, 16.5) * mm});
            skPoint(sketch, "E22.middle", {"position": v(-80, 17.5) * mm});
            skCircle(sketch, "E23", {"center": v(-74, -20) * mm, "radius": 1 * mm});
            skLineSegment(sketch, "E24.bottom", {"start": v(-76.5, -18.5) * mm, "end": v(-83.5, -18.5) * mm});
            skLineSegment(sketch, "E24.top", {"start": v(-76.5, -16.63) * mm, "end": v(-83.5, -16.63) * mm});
            skLineSegment(sketch, "E24.left", {"start": v(-76.5, -18.5) * mm, "end": v(-76.5, -16.63) * mm});
            skLineSegment(sketch, "E24.right", {"start": v(-83.5, -18.5) * mm, "end": v(-83.5, -16.63) * mm});
            skPoint(sketch, "E24.middle", {"position": v(-80, -17.56) * mm});
            skLineSegment(sketch, "E25.bottom", {"start": v(-76.5, -21.5) * mm, "end": v(-83.5, -21.5) * mm});
            skLineSegment(sketch, "E25.top", {"start": v(-76.5, -23.67) * mm, "end": v(-83.5, -23.67) * mm});
            skLineSegment(sketch, "E25.left", {"start": v(-76.5, -21.5) * mm, "end": v(-76.5, -23.67) * mm});
            skLineSegment(sketch, "E25.right", {"start": v(-83.5, -21.5) * mm, "end": v(-83.5, -23.67) * mm});
            skPoint(sketch, "E25.middle", {"position": v(-80, -22.58) * mm});
            skCircle(sketch, "E26", {"center": v(-86, -20) * mm, "radius": 1 * mm});
            skSolve(sketch);
        }
        {
            var Q0;
            Q0 = qSketchRegion(id + "F6", true);
            extrude(context, id + "F7", {"entities" : qUnion([Q0]), "operationType" : NewBodyOperationType.REMOVE, "oppositeDirection" : true, "depth" : 2 * mm});
        }
        {
            var Q0;
            Q0=makeQuery(id+"F1.opExtrude","CAP_FACE",FACE,{"disambiguationData":[OSD([sQuery(id+"F0.wireOp",EDGE,"E0.bottom"),sQuery(id+"F0.wireOp",EDGE,"E0.top"),sQuery(id+"F0.wireOp",EDGE,"E0.left"),sQuery(id+"F0.wireOp",EDGE,"E0.right")])],"isStart":false});
            var sketch = newSketch(context, id + "F8", { "sketchPlane" : qUnion([Q0])});
            skLineSegment(sketch, "E27.bottom", {"start": v(-70.25, 30) * mm, "end": v(-69.75, 30) * mm});
            skLineSegment(sketch, "E27.top", {"start": v(-70.25, -30) * mm, "end": v(-69.75, -30) * mm});
            skLineSegment(sketch, "E27.left", {"start": v(-70.25, 30) * mm, "end": v(-70.25, -30) * mm});
            skLineSegment(sketch, "E27.right", {"start": v(-69.75, 30) * mm, "end": v(-69.75, -30) * mm});
            skLineSegment(sketch, "E28.1.0.0", {"start": v(-50.25, 30) * mm, "end": v(-50.25, -30) * mm});
            skLineSegment(sketch, "E28.1.0.1", {"start": v(-49.75, 30) * mm, "end": v(-49.75, -30) * mm});
            skLineSegment(sketch, "E28.1.0.2", {"start": v(-50.25, -30) * mm, "end": v(-49.75, -30) * mm});
            skLineSegment(sketch, "E28.1.0.3", {"start": v(-50.25, 30) * mm, "end": v(-49.75, 30) * mm});
            skLineSegment(sketch, "E28.2.0.0", {"start": v(-30.25, 30) * mm, "end": v(-30.25, -30) * mm});
            skLineSegment(sketch, "E28.2.0.1", {"start": v(-29.75, 30) * mm, "end": v(-29.75, -30) * mm});
            skLineSegment(sketch, "E28.2.0.2", {"start": v(-30.25, -30) * mm, "end": v(-29.75, -30) * mm});
            skLineSegment(sketch, "E28.2.0.3", {"start": v(-30.25, 30) * mm, "end": v(-29.75, 30) * mm});
            skLineSegment(sketch, "E28.3.0.0", {"start": v(-10.25, 30) * mm, "end": v(-10.25, -30) * mm});
            skLineSegment(sketch, "E28.3.0.1", {"start": v(-9.75, 30) * mm, "end": v(-9.75, -30) * mm});
            skLineSegment(sketch, "E28.3.0.2", {"start": v(-10.25, -30) * mm, "end": v(-9.75, -30) * mm});
            skLineSegment(sketch, "E28.3.0.3", {"start": v(-10.25, 30) * mm, "end": v(-9.75, 30) * mm});
            skLineSegment(sketch, "E28.4.0.0", {"start": v(9.75, 30) * mm, "end": v(9.75, -30) * mm});
            skLineSegment(sketch, "E28.4.0.1", {"start": v(10.25, 30) * mm, "end": v(10.25, -30) * mm});
            skLineSegment(sketch, "E28.4.0.2", {"start": v(9.75, -30) * mm, "end": v(10.25, -30) * mm});
            skLineSegment(sketch, "E28.4.0.3", {"start": v(9.75, 30) * mm, "end": v(10.25, 30) * mm});
            skLineSegment(sketch, "E28.5.0.0", {"start": v(29.75, 30) * mm, "end": v(29.75, -30) * mm});
            skLineSegment(sketch, "E28.5.0.1", {"start": v(30.25, 30) * mm, "end": v(30.25, -30) * mm});
            skLineSegment(sketch, "E28.5.0.2", {"start": v(29.75, -30) * mm, "end": v(30.25, -30) * mm});
            skLineSegment(sketch, "E28.5.0.3", {"start": v(29.75, 30) * mm, "end": v(30.25, 30) * mm});
            skLineSegment(sketch, "E28.6.0.0", {"start": v(49.75, 30) * mm, "end": v(49.75, -30) * mm});
            skLineSegment(sketch, "E28.6.0.1", {"start": v(50.25, 30) * mm, "end": v(50.25, -30) * mm});
            skLineSegment(sketch, "E28.6.0.2", {"start": v(49.75, -30) * mm, "end": v(50.25, -30) * mm});
            skLineSegment(sketch, "E28.6.0.3", {"start": v(49.75, 30) * mm, "end": v(50.25, 30) * mm});
            skLineSegment(sketch, "E28.7.0.0", {"start": v(69.75, 30) * mm, "end": v(69.75, -30) * mm});
            skLineSegment(sketch, "E28.7.0.1", {"start": v(70.25, 30) * mm, "end": v(70.25, -30) * mm});
            skLineSegment(sketch, "E28.7.0.2", {"start": v(69.75, -30) * mm, "end": v(70.25, -30) * mm});
            skLineSegment(sketch, "E28.7.0.3", {"start": v(69.75, 30) * mm, "end": v(70.25, 30) * mm});
            skLineSegment(sketch, "E28.direction1", {"start": v(-70.25, -30) * mm, "end": v(-50.25, -30) * mm, "construction": true});
            skSolve(sketch);
        }
        {
            var Q0;
            Q0 = qSketchRegion(id + "F8", true);
            extrude(context, id + "F9", {"entities" : qUnion([Q0]), "operationType" : NewBodyOperationType.ADD, "depth" : 1 * mm});
        }
    });
